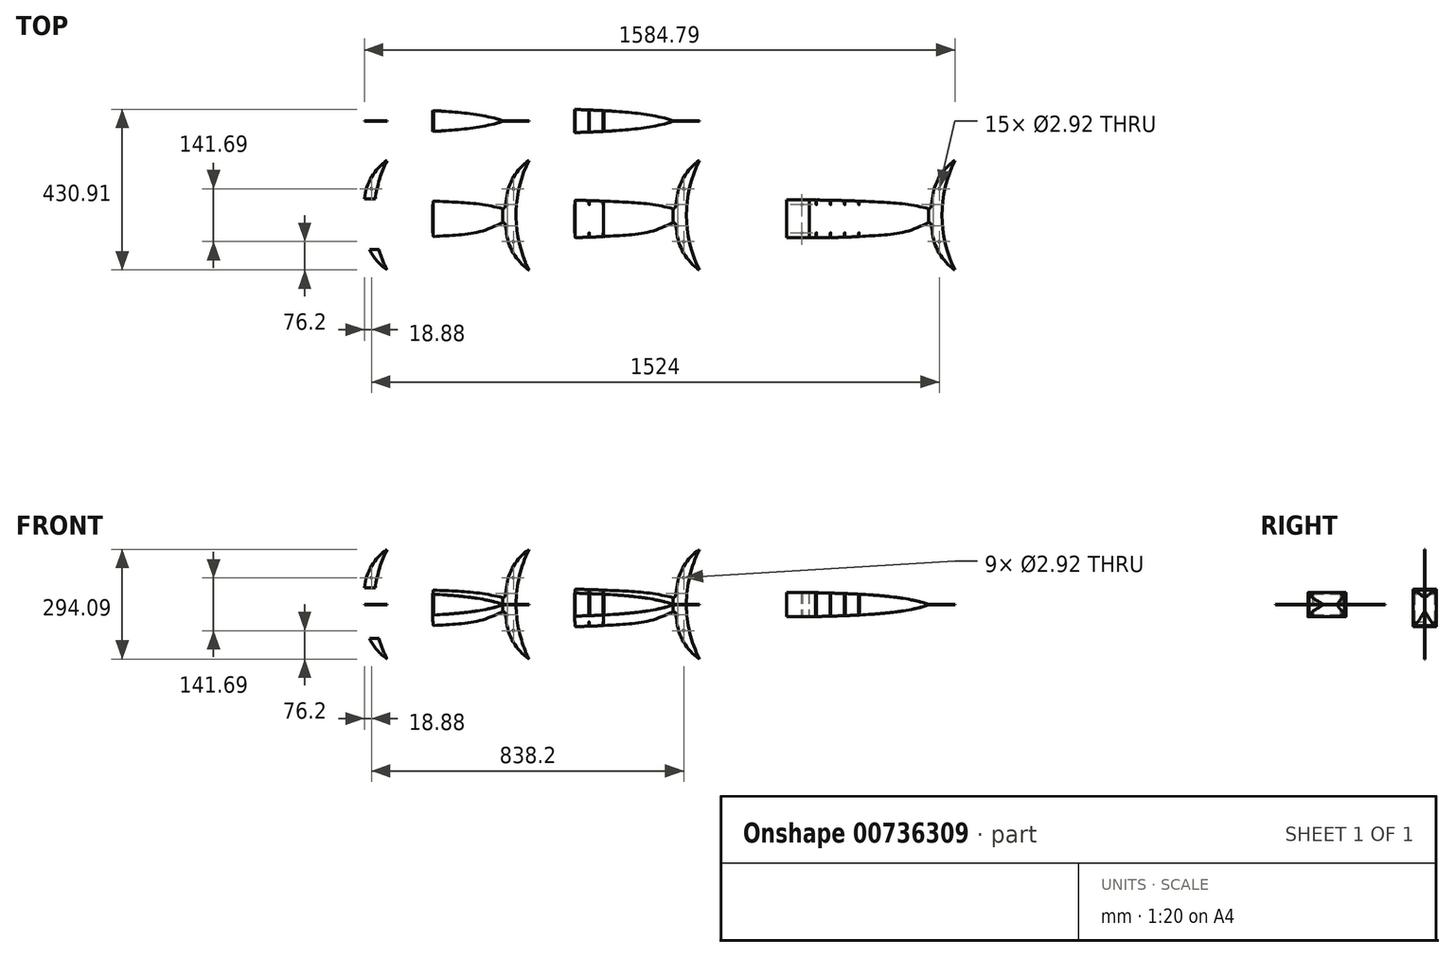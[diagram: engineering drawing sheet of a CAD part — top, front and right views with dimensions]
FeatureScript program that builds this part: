
annotation { "Feature Type Name" : "Feature", "Feature Type Description" : "" }
export const myFeature = defineFeature(function(context is Context, id is Id, definition is map)
    precondition{}
    {
        {
            var Q0;
            Q0=qCreatedBy(makeId("Top.planeOp"),FACE);
            var sketch = newSketch(context, id + "F0", { "sketchPlane" : qUnion([Q0])});
            skArc(sketch, "E0", {"start": v(-213.15, 1.58) * mm, "mid": v(-216.75, 0.09) * mm, "end": v(-218.23, -3.5) * mm});
            skLineSegment(sketch, "E1", {"start": v(-213.15, -100.02) * mm, "end": v(-116.63, -100.02) * mm});
            skLineSegment(sketch, "E2", {"start": v(-218.23, -3.5) * mm, "end": v(-218.23, -94.94) * mm});
            skArc(sketch, "E3", {"start": v(-218.23, -94.94) * mm, "mid": v(-216.75, -98.53) * mm, "end": v(-213.15, -100.02) * mm});
            skArc(sketch, "E4", {"start": v(274.89, 107.35) * mm, "mid": v(233.7, 63.25) * mm, "end": v(214.38, 6.08) * mm});
            skArc(sketch, "E5", {"start": v(214, -81.56) * mm, "mid": v(232.7, -140.95) * mm, "end": v(274.89, -186.74) * mm});
            skArc(sketch, "E6", {"start": v(274.89, 107.35) * mm, "mid": v(240.22, -39.7) * mm, "end": v(274.89, -186.74) * mm});
            skCircle(sketch, "E7", {"center": v(-199.18, -11.12) * mm, "radius": 1.46 * mm});
            skCircle(sketch, "E8", {"center": v(-199.18, -87.32) * mm, "radius": 1.46 * mm});
            skCircle(sketch, "E9", {"center": v(-135.68, -11.12) * mm, "radius": 1.46 * mm});
            skCircle(sketch, "E10", {"center": v(-135.68, -87.32) * mm, "radius": 1.46 * mm});
            skCircle(sketch, "E11", {"center": v(216.74, -11.22) * mm, "radius": 1.46 * mm});
            skCircle(sketch, "E12", {"center": v(216.74, -68.27) * mm, "radius": 1.46 * mm});
            skCircle(sketch, "E13", {"center": v(232.98, 31.15) * mm, "radius": 1.46 * mm});
            skCircle(sketch, "E14", {"center": v(232.98, -110.54) * mm, "radius": 1.46 * mm});
            skLineSegment(sketch, "E15", {"start": v(-116.63, 1.58) * mm, "end": v(-213.15, 1.58) * mm});
            skFitSpline(sketch, "E16", {"points": [v(-116.63, 1.58) * mm, v(-110.7, 1.48) * mm, v(-104.77, 1.39) * mm, v(-98.83, 1.29) * mm]});
            skFitSpline(sketch, "E17", {"points": [v(-95.28, 1.23) * mm, v(-83.76, 1.03) * mm, v(-72.24, 0.83) * mm, v(-60.73, 0.58) * mm]});
            skFitSpline(sketch, "E18", {"points": [v(-57.17, 0.5) * mm, v(-45.64, 0.25) * mm, v(-34.12, -0.04) * mm, v(-22.61, -0.39) * mm]});
            skFitSpline(sketch, "E19", {"points": [v(-19.06, -0.5) * mm, v(-7.53, -0.86) * mm, v(4, -1.29) * mm, v(15.5, -1.8) * mm]});
            skFitSpline(sketch, "E20", {"points": [v(19.06, -1.96) * mm, v(81.46, -4.83) * mm, v(143.45, -10.28) * mm, v(204.47, -21.88) * mm]});
            skFitSpline(sketch, "E21", {"points": [v(-116.63, -100.02) * mm, v(-110.7, -100) * mm, v(-104.77, -99.97) * mm, v(-98.85, -99.94) * mm]});
            skFitSpline(sketch, "E22", {"points": [v(-95.3, -99.92) * mm, v(-83.76, -99.85) * mm, v(-72.24, -99.76) * mm, v(-60.74, -99.6) * mm]});
            skFitSpline(sketch, "E23", {"points": [v(-57.18, -99.55) * mm, v(-45.63, -99.37) * mm, v(-34.1, -99.11) * mm, v(-22.61, -98.74) * mm]});
            skFitSpline(sketch, "E24", {"points": [v(-19.05, -98.62) * mm, v(-7.48, -98.22) * mm, v(4.05, -97.7) * mm, v(15.52, -97) * mm]});
            skFitSpline(sketch, "E25", {"points": [v(19.08, -96.77) * mm, v(83.42, -92.65) * mm, v(145.93, -83) * mm, v(204.03, -59.86) * mm]});
            skLineSegment(sketch, "E26", {"start": v(214.38, 6.08) * mm, "end": v(210.43, -17.72) * mm});
            skLineSegment(sketch, "E27", {"start": v(210.92, -63.72) * mm, "end": v(214, -81.56) * mm});
            skArc(sketch, "E28", {"start": v(204.47, -21.88) * mm, "mid": v(208.32, -21.06) * mm, "end": v(210.43, -17.72) * mm});
            skArc(sketch, "E29", {"start": v(210.92, -63.72) * mm, "mid": v(208.4, -60.15) * mm, "end": v(204.03, -59.86) * mm});
            skLineSegment(sketch, "E30", {"start": v(-97.58, -11.12) * mm, "end": v(-97.58, 0.02) * mm});
            skLineSegment(sketch, "E31", {"start": v(-96.57, -11.12) * mm, "end": v(-96.57, -0.04) * mm});
            skArc(sketch, "E32", {"start": v(-97.58, -11.12) * mm, "mid": v(-97.08, -11.63) * mm, "end": v(-96.57, -11.12) * mm});
            skArc(sketch, "E33", {"start": v(-97.58, 0.02) * mm, "mid": v(-97.95, 0.9) * mm, "end": v(-98.83, 1.29) * mm});
            skArc(sketch, "E34", {"start": v(-95.28, 1.23) * mm, "mid": v(-96.19, 0.86) * mm, "end": v(-96.57, -0.04) * mm});
            skLineSegment(sketch, "E35", {"start": v(-97.58, -87.32) * mm, "end": v(-97.58, -98.67) * mm});
            skLineSegment(sketch, "E36", {"start": v(-96.57, -87.32) * mm, "end": v(-96.57, -98.65) * mm});
            skArc(sketch, "E37", {"start": v(-96.57, -87.32) * mm, "mid": v(-97.08, -86.81) * mm, "end": v(-97.58, -87.32) * mm});
            skArc(sketch, "E38", {"start": v(-98.85, -99.94) * mm, "mid": v(-97.95, -99.57) * mm, "end": v(-97.58, -98.67) * mm});
            skArc(sketch, "E39", {"start": v(-96.57, -98.65) * mm, "mid": v(-96.2, -99.55) * mm, "end": v(-95.3, -99.92) * mm});
            skLineSegment(sketch, "E40", {"start": v(-59.48, -11.12) * mm, "end": v(-59.48, -0.69) * mm});
            skLineSegment(sketch, "E41", {"start": v(-58.47, -11.12) * mm, "end": v(-58.47, -0.76) * mm});
            skArc(sketch, "E42", {"start": v(-59.48, -11.12) * mm, "mid": v(-58.98, -11.63) * mm, "end": v(-58.47, -11.12) * mm});
            skArc(sketch, "E43", {"start": v(-59.48, -0.69) * mm, "mid": v(-59.85, 0.2) * mm, "end": v(-60.73, 0.58) * mm});
            skArc(sketch, "E44", {"start": v(-57.17, 0.5) * mm, "mid": v(-58.09, 0.14) * mm, "end": v(-58.47, -0.76) * mm});
            skLineSegment(sketch, "E45", {"start": v(-59.48, -87.32) * mm, "end": v(-59.48, -98.33) * mm});
            skLineSegment(sketch, "E46", {"start": v(-58.47, -87.32) * mm, "end": v(-58.47, -98.28) * mm});
            skArc(sketch, "E47", {"start": v(-58.47, -87.32) * mm, "mid": v(-58.98, -86.81) * mm, "end": v(-59.48, -87.32) * mm});
            skArc(sketch, "E48", {"start": v(-60.74, -99.6) * mm, "mid": v(-59.85, -99.22) * mm, "end": v(-59.48, -98.33) * mm});
            skArc(sketch, "E49", {"start": v(-58.47, -98.28) * mm, "mid": v(-58.09, -99.18) * mm, "end": v(-57.18, -99.55) * mm});
            skLineSegment(sketch, "E50", {"start": v(-21.38, -11.12) * mm, "end": v(-21.38, -1.65) * mm});
            skLineSegment(sketch, "E51", {"start": v(-20.37, -11.12) * mm, "end": v(-20.37, -1.77) * mm});
            skLineSegment(sketch, "E52", {"start": v(-21.38, -87.32) * mm, "end": v(-21.38, -97.47) * mm});
            skLineSegment(sketch, "E53", {"start": v(-20.37, -87.32) * mm, "end": v(-20.37, -97.35) * mm});
            skLineSegment(sketch, "E54", {"start": v(16.72, -11.12) * mm, "end": v(16.72, -3.07) * mm});
            skLineSegment(sketch, "E55", {"start": v(17.73, -11.12) * mm, "end": v(17.73, -3.23) * mm});
            skLineSegment(sketch, "E56", {"start": v(16.72, -87.32) * mm, "end": v(16.72, -95.73) * mm});
            skLineSegment(sketch, "E57", {"start": v(17.73, -87.32) * mm, "end": v(17.73, -95.5) * mm});
            skArc(sketch, "E58", {"start": v(-21.38, -11.12) * mm, "mid": v(-20.88, -11.63) * mm, "end": v(-20.37, -11.12) * mm});
            skArc(sketch, "E59", {"start": v(16.72, -11.12) * mm, "mid": v(17.22, -11.63) * mm, "end": v(17.73, -11.12) * mm});
            skArc(sketch, "E60", {"start": v(17.73, -87.32) * mm, "mid": v(17.22, -86.81) * mm, "end": v(16.72, -87.32) * mm});
            skArc(sketch, "E61", {"start": v(-20.37, -87.32) * mm, "mid": v(-20.88, -86.81) * mm, "end": v(-21.38, -87.32) * mm});
            skArc(sketch, "E62", {"start": v(-19.06, -0.5) * mm, "mid": v(-19.98, -0.85) * mm, "end": v(-20.37, -1.77) * mm});
            skArc(sketch, "E63", {"start": v(-21.38, -1.65) * mm, "mid": v(-21.74, -0.77) * mm, "end": v(-22.61, -0.39) * mm});
            skArc(sketch, "E64", {"start": v(16.72, -3.07) * mm, "mid": v(16.36, -2.19) * mm, "end": v(15.5, -1.8) * mm});
            skArc(sketch, "E65", {"start": v(19.06, -1.96) * mm, "mid": v(18.13, -2.3) * mm, "end": v(17.73, -3.23) * mm});
            skArc(sketch, "E66", {"start": v(15.52, -97) * mm, "mid": v(16.37, -96.6) * mm, "end": v(16.72, -95.73) * mm});
            skArc(sketch, "E67", {"start": v(17.73, -95.5) * mm, "mid": v(18.13, -96.43) * mm, "end": v(19.08, -96.77) * mm});
            skArc(sketch, "E68", {"start": v(-22.61, -98.74) * mm, "mid": v(-21.74, -98.36) * mm, "end": v(-21.38, -97.47) * mm});
            skArc(sketch, "E69", {"start": v(-20.37, -97.35) * mm, "mid": v(-19.98, -98.27) * mm, "end": v(-19.05, -98.62) * mm});
            skArc(sketch, "E70", {"start": v(201.54, 0.54) * mm, "mid": v(204.92, 1.83) * mm, "end": v(206.59, 5.04) * mm});
            skLineSegment(sketch, "E71", {"start": v(206.62, 5.62) * mm, "end": v(206.62, 97.06) * mm});
            skCircle(sketch, "E72", {"center": v(187.57, 13.24) * mm, "radius": 1.46 * mm});
            skCircle(sketch, "E73", {"center": v(124.07, 13.24) * mm, "radius": 1.46 * mm});
            skLineSegment(sketch, "E74", {"start": v(105.02, 0.54) * mm, "end": v(201.54, 0.54) * mm});
            skFitSpline(sketch, "E75", {"points": [v(105.02, 0.54) * mm, v(99.09, 0.63) * mm, v(93.15, 0.73) * mm, v(87.22, 0.83) * mm]});
            skFitSpline(sketch, "E76", {"points": [v(83.66, 0.89) * mm, v(72.14, 1.08) * mm, v(60.63, 1.29) * mm, v(49.11, 1.53) * mm]});
            skFitSpline(sketch, "E77", {"points": [v(45.56, 1.6) * mm, v(34.03, 1.86) * mm, v(22.51, 2.15) * mm, v(11, 2.5) * mm]});
            skFitSpline(sketch, "E78", {"points": [v(7.44, 2.6) * mm, v(-4.09, 2.97) * mm, v(-15.6, 3.4) * mm, v(-27.12, 3.91) * mm]});
            skLineSegment(sketch, "E79", {"start": v(-226, -3.97) * mm, "end": v(-222.04, 19.84) * mm});
            skLineSegment(sketch, "E80", {"start": v(85.97, 13.24) * mm, "end": v(85.97, 2.1) * mm});
            skLineSegment(sketch, "E81", {"start": v(84.95, 13.24) * mm, "end": v(84.95, 2.16) * mm});
            skArc(sketch, "E82", {"start": v(85.97, 13.24) * mm, "mid": v(85.46, 13.74) * mm, "end": v(84.95, 13.24) * mm});
            skArc(sketch, "E83", {"start": v(85.97, 2.1) * mm, "mid": v(86.34, 1.2) * mm, "end": v(87.22, 0.83) * mm});
            skArc(sketch, "E84", {"start": v(83.66, 0.89) * mm, "mid": v(84.58, 1.25) * mm, "end": v(84.95, 2.16) * mm});
            skLineSegment(sketch, "E85", {"start": v(47.87, 13.24) * mm, "end": v(47.87, 2.8) * mm});
            skLineSegment(sketch, "E86", {"start": v(46.85, 13.24) * mm, "end": v(46.85, 2.88) * mm});
            skArc(sketch, "E87", {"start": v(47.87, 13.24) * mm, "mid": v(47.36, 13.74) * mm, "end": v(46.85, 13.24) * mm});
            skArc(sketch, "E88", {"start": v(47.87, 2.8) * mm, "mid": v(48.23, 1.91) * mm, "end": v(49.11, 1.53) * mm});
            skArc(sketch, "E89", {"start": v(45.56, 1.6) * mm, "mid": v(46.47, 1.97) * mm, "end": v(46.85, 2.88) * mm});
            skLineSegment(sketch, "E90", {"start": v(9.77, 13.24) * mm, "end": v(9.77, 3.77) * mm});
            skLineSegment(sketch, "E91", {"start": v(8.75, 13.24) * mm, "end": v(8.75, 3.88) * mm});
            skLineSegment(sketch, "E92", {"start": v(-28.33, 13.24) * mm, "end": v(-28.33, 5.18) * mm});
            skLineSegment(sketch, "E93", {"start": v(-29.35, 13.24) * mm, "end": v(-29.35, 5.34) * mm});
            skArc(sketch, "E94", {"start": v(9.77, 13.24) * mm, "mid": v(9.26, 13.74) * mm, "end": v(8.75, 13.24) * mm});
            skArc(sketch, "E95", {"start": v(-28.33, 13.24) * mm, "mid": v(-28.84, 13.74) * mm, "end": v(-29.35, 13.24) * mm});
            skArc(sketch, "E96", {"start": v(7.44, 2.6) * mm, "mid": v(8.37, 2.97) * mm, "end": v(8.75, 3.88) * mm});
            skArc(sketch, "E97", {"start": v(9.77, 3.77) * mm, "mid": v(10.13, 2.88) * mm, "end": v(11, 2.5) * mm});
            skArc(sketch, "E98", {"start": v(-28.33, 5.18) * mm, "mid": v(-27.98, 4.3) * mm, "end": v(-27.12, 3.91) * mm});
            skArc(sketch, "E99", {"start": v(-30.67, 4.07) * mm, "mid": v(-29.74, 4.42) * mm, "end": v(-29.35, 5.34) * mm});
            skSolve(sketch);
        }
        {
            var Q0;
            Q0 = qSketchRegion(id + "F0", true);
            extrude(context, id + "F1", {"entities" : qUnion([Q0]), "depth" : 32.5 * mm, "offsetDistance" : 25.4 * mm});
        }
        {
            var Q0;
            Q0=makeQuery(id+"F1.opExtrude","SWEPT_BODY",BODY,{"disambiguationData":[OSD([sQuery(id+"F0.wireOp",EDGE,"E72")])]});
            var Q1;
            Q1=makeQuery(id+"F1.opExtrude","SWEPT_BODY",BODY,{"disambiguationData":[OSD([sQuery(id+"F0.wireOp",EDGE,"E73")])]});
            deleteBodies(context, id + "F2", {"entities" : qUnion([Q0, Q1])});
        }
        {
            var Q0;
            Q0=qCreatedBy(makeId("Front.planeOp"),FACE);
            var sketch = newSketch(context, id + "F3", { "sketchPlane" : qUnion([Q0])});
            skLineSegment(sketch, "E100.0", {"start": v(274.89, 0) * mm, "end": v(214.38, 0) * mm});
            skLineSegment(sketch, "E101.0", {"start": v(204.47, 0) * mm, "end": v(210.43, 0) * mm});
            skLineSegment(sketch, "E102.0", {"start": v(214.38, 0) * mm, "end": v(210.43, 0) * mm});
            skLineSegment(sketch, "E103.0", {"start": v(-213.15, 32.51) * mm, "end": v(-218.23, 32.51) * mm});
            skLineSegment(sketch, "E104.0", {"start": v(-116.63, 32.51) * mm, "end": v(-213.15, 32.51) * mm});
            skLineSegment(sketch, "E105", {"start": v(-218.23, 32.51) * mm, "end": v(-218.23, 31.75) * mm});
            skLineSegment(sketch, "E106", {"start": v(-218.23, 31.75) * mm, "end": v(-116.63, 31.75) * mm});
            skLineSegment(sketch, "E107", {"start": v(274.89, 0) * mm, "end": v(274.89, 0.76) * mm});
            skLineSegment(sketch, "E108", {"start": v(274.89, 0.76) * mm, "end": v(204.47, 0.76) * mm});
            skFitSpline(sketch, "E109", {"points": [v(-116.63, 32.51) * mm, v(204.47, 0.76) * mm, v(299.9, -60.17) * mm], "startDerivative": vector(591.31, -15) * mm, "endDerivative": vector(209.17, -184.85) * mm});
            skFitSpline(sketch, "E110.0", {"points": [v(-116.65, 31.75) * mm, v(-92.01, 31.12) * mm, v(-42.74, 29.87) * mm, v(28.78, 26.94) * mm, v(95.52, 21.9) * mm, v(145.19, 15.06) * mm, v(180.14, 7.48) * mm, v(203.67, 0.62) * mm, v(224.2, -7.56) * mm, v(248.23, -19.95) * mm, v(273.28, -37.65) * mm, v(290.69, -53.04) * mm, v(299.4, -60.74) * mm]});
            skLineSegment(sketch, "E111", {"start": v(204.22, 0.04) * mm, "end": v(204.47, 0) * mm});
            skLineSegment(sketch, "E112.0", {"start": v(-218.23, 32.51) * mm, "end": v(-218.23, 0) * mm});
            skLineSegment(sketch, "E113", {"start": v(-218.23, 0) * mm, "end": v(204.47, 0) * mm});
            skLineSegment(sketch, "E114", {"start": v(-116.63, 32.51) * mm, "end": v(275.65, 32.51) * mm});
            skLineSegment(sketch, "E115", {"start": v(275.65, 32.51) * mm, "end": v(275.65, -7.5) * mm});
            skLineSegment(sketch, "E116", {"start": v(274.89, 0) * mm, "end": v(275.65, 0) * mm});
            skSolve(sketch);
        }
        {
            var Q0;
            Q0=makeQuery(id+"F3.imprint","IMPRINT",FACE,{"disambiguationData":[TD([[makeQuery(id+"F3.imprint","IMPRINT",EDGE,{"derivedFrom":sQuery(id+"F3.wireOp",EDGE,"E107")}),-1.0]])]});
            var Q1;
            {var subQ4=sQuery(id+"F3.wireOp",EDGE,"E111");Q1=makeQuery(id+"F3.imprint","IMPRINT",FACE,{"disambiguationData":[TD([[makeQuery(id+"F3.imprint","IMPRINT",EDGE,{"derivedFrom":subQ4}),-1.0]])]});}
            extrude(context, id + "F4", {"entities" : qUnion([Q0, Q1]), "operationType" : NewBodyOperationType.REMOVE, "endBound" : BoundingType.SYMMETRIC, "oppositeDirection" : true, "depth" : 508 * mm, "offsetDistance" : 25.4 * mm});
        }
        {
            var Q0;
            Q0=makeQuery(id+"F1.opExtrude","SWEPT_BODY",BODY,{"disambiguationData":[OSD([sQuery(id+"F0.wireOp",EDGE,"E0"),sQuery(id+"F0.wireOp",EDGE,"E1"),sQuery(id+"F0.wireOp",EDGE,"E2"),sQuery(id+"F0.wireOp",EDGE,"E3"),sQuery(id+"F0.wireOp",EDGE,"E4"),sQuery(id+"F0.wireOp",EDGE,"E5"),sQuery(id+"F0.wireOp",EDGE,"E6"),sQuery(id+"F0.wireOp",EDGE,"E7"),sQuery(id+"F0.wireOp",EDGE,"E8"),sQuery(id+"F0.wireOp",EDGE,"E9"),sQuery(id+"F0.wireOp",EDGE,"E10"),sQuery(id+"F0.wireOp",EDGE,"E11"),sQuery(id+"F0.wireOp",EDGE,"E12"),sQuery(id+"F0.wireOp",EDGE,"E13"),sQuery(id+"F0.wireOp",EDGE,"E14"),sQuery(id+"F0.wireOp",EDGE,"E15"),sQuery(id+"F0.wireOp",EDGE,"E16"),sQuery(id+"F0.wireOp",EDGE,"E17"),sQuery(id+"F0.wireOp",EDGE,"E18"),sQuery(id+"F0.wireOp",EDGE,"E19"),sQuery(id+"F0.wireOp",EDGE,"E20"),sQuery(id+"F0.wireOp",EDGE,"E21"),sQuery(id+"F0.wireOp",EDGE,"E22"),sQuery(id+"F0.wireOp",EDGE,"E23"),sQuery(id+"F0.wireOp",EDGE,"E24"),sQuery(id+"F0.wireOp",EDGE,"E25"),sQuery(id+"F0.wireOp",EDGE,"E26"),sQuery(id+"F0.wireOp",EDGE,"E27"),sQuery(id+"F0.wireOp",EDGE,"E28"),sQuery(id+"F0.wireOp",EDGE,"E29"),sQuery(id+"F0.wireOp",EDGE,"E30"),sQuery(id+"F0.wireOp",EDGE,"E31"),sQuery(id+"F0.wireOp",EDGE,"E32"),sQuery(id+"F0.wireOp",EDGE,"E33"),sQuery(id+"F0.wireOp",EDGE,"E34"),sQuery(id+"F0.wireOp",EDGE,"E35"),sQuery(id+"F0.wireOp",EDGE,"E36"),sQuery(id+"F0.wireOp",EDGE,"E37"),sQuery(id+"F0.wireOp",EDGE,"E38"),sQuery(id+"F0.wireOp",EDGE,"E39"),sQuery(id+"F0.wireOp",EDGE,"E40"),sQuery(id+"F0.wireOp",EDGE,"E41"),sQuery(id+"F0.wireOp",EDGE,"E42"),sQuery(id+"F0.wireOp",EDGE,"E43"),sQuery(id+"F0.wireOp",EDGE,"E44"),sQuery(id+"F0.wireOp",EDGE,"E45"),sQuery(id+"F0.wireOp",EDGE,"E46"),sQuery(id+"F0.wireOp",EDGE,"E47"),sQuery(id+"F0.wireOp",EDGE,"E48"),sQuery(id+"F0.wireOp",EDGE,"E49"),sQuery(id+"F0.wireOp",EDGE,"E50"),sQuery(id+"F0.wireOp",EDGE,"E51"),sQuery(id+"F0.wireOp",EDGE,"E52"),sQuery(id+"F0.wireOp",EDGE,"E53"),sQuery(id+"F0.wireOp",EDGE,"E54"),sQuery(id+"F0.wireOp",EDGE,"E55"),sQuery(id+"F0.wireOp",EDGE,"E56"),sQuery(id+"F0.wireOp",EDGE,"E57"),sQuery(id+"F0.wireOp",EDGE,"E58"),sQuery(id+"F0.wireOp",EDGE,"E59"),sQuery(id+"F0.wireOp",EDGE,"E60"),sQuery(id+"F0.wireOp",EDGE,"E61"),sQuery(id+"F0.wireOp",EDGE,"E62"),sQuery(id+"F0.wireOp",EDGE,"E63"),sQuery(id+"F0.wireOp",EDGE,"E64"),sQuery(id+"F0.wireOp",EDGE,"E65"),sQuery(id+"F0.wireOp",EDGE,"E66"),sQuery(id+"F0.wireOp",EDGE,"E67"),sQuery(id+"F0.wireOp",EDGE,"E68"),sQuery(id+"F0.wireOp",EDGE,"E69")])]});
            var Q1;
            Q1=makeQuery(id+"F1.opExtrude","CAP_FACE",FACE,{"disambiguationData":[OSD([sQuery(id+"F0.wireOp",EDGE,"E0"),sQuery(id+"F0.wireOp",EDGE,"E1"),sQuery(id+"F0.wireOp",EDGE,"E2"),sQuery(id+"F0.wireOp",EDGE,"E3"),sQuery(id+"F0.wireOp",EDGE,"E4"),sQuery(id+"F0.wireOp",EDGE,"E5"),sQuery(id+"F0.wireOp",EDGE,"E6"),sQuery(id+"F0.wireOp",EDGE,"E7"),sQuery(id+"F0.wireOp",EDGE,"E8"),sQuery(id+"F0.wireOp",EDGE,"E9"),sQuery(id+"F0.wireOp",EDGE,"E10"),sQuery(id+"F0.wireOp",EDGE,"E11"),sQuery(id+"F0.wireOp",EDGE,"E12"),sQuery(id+"F0.wireOp",EDGE,"E13"),sQuery(id+"F0.wireOp",EDGE,"E14"),sQuery(id+"F0.wireOp",EDGE,"E15"),sQuery(id+"F0.wireOp",EDGE,"E16"),sQuery(id+"F0.wireOp",EDGE,"E17"),sQuery(id+"F0.wireOp",EDGE,"E18"),sQuery(id+"F0.wireOp",EDGE,"E19"),sQuery(id+"F0.wireOp",EDGE,"E20"),sQuery(id+"F0.wireOp",EDGE,"E21"),sQuery(id+"F0.wireOp",EDGE,"E22"),sQuery(id+"F0.wireOp",EDGE,"E23"),sQuery(id+"F0.wireOp",EDGE,"E24"),sQuery(id+"F0.wireOp",EDGE,"E25"),sQuery(id+"F0.wireOp",EDGE,"E26"),sQuery(id+"F0.wireOp",EDGE,"E27"),sQuery(id+"F0.wireOp",EDGE,"E28"),sQuery(id+"F0.wireOp",EDGE,"E29"),sQuery(id+"F0.wireOp",EDGE,"E30"),sQuery(id+"F0.wireOp",EDGE,"E31"),sQuery(id+"F0.wireOp",EDGE,"E32"),sQuery(id+"F0.wireOp",EDGE,"E33"),sQuery(id+"F0.wireOp",EDGE,"E34"),sQuery(id+"F0.wireOp",EDGE,"E35"),sQuery(id+"F0.wireOp",EDGE,"E36"),sQuery(id+"F0.wireOp",EDGE,"E37"),sQuery(id+"F0.wireOp",EDGE,"E38"),sQuery(id+"F0.wireOp",EDGE,"E39"),sQuery(id+"F0.wireOp",EDGE,"E40"),sQuery(id+"F0.wireOp",EDGE,"E41"),sQuery(id+"F0.wireOp",EDGE,"E42"),sQuery(id+"F0.wireOp",EDGE,"E43"),sQuery(id+"F0.wireOp",EDGE,"E44"),sQuery(id+"F0.wireOp",EDGE,"E45"),sQuery(id+"F0.wireOp",EDGE,"E46"),sQuery(id+"F0.wireOp",EDGE,"E47"),sQuery(id+"F0.wireOp",EDGE,"E48"),sQuery(id+"F0.wireOp",EDGE,"E49"),sQuery(id+"F0.wireOp",EDGE,"E50"),sQuery(id+"F0.wireOp",EDGE,"E51"),sQuery(id+"F0.wireOp",EDGE,"E52"),sQuery(id+"F0.wireOp",EDGE,"E53"),sQuery(id+"F0.wireOp",EDGE,"E54"),sQuery(id+"F0.wireOp",EDGE,"E55"),sQuery(id+"F0.wireOp",EDGE,"E56"),sQuery(id+"F0.wireOp",EDGE,"E57"),sQuery(id+"F0.wireOp",EDGE,"E58"),sQuery(id+"F0.wireOp",EDGE,"E59"),sQuery(id+"F0.wireOp",EDGE,"E60"),sQuery(id+"F0.wireOp",EDGE,"E61"),sQuery(id+"F0.wireOp",EDGE,"E62"),sQuery(id+"F0.wireOp",EDGE,"E63"),sQuery(id+"F0.wireOp",EDGE,"E64"),sQuery(id+"F0.wireOp",EDGE,"E65"),sQuery(id+"F0.wireOp",EDGE,"E66"),sQuery(id+"F0.wireOp",EDGE,"E67"),sQuery(id+"F0.wireOp",EDGE,"E68"),sQuery(id+"F0.wireOp",EDGE,"E69")])],"isStart":true});
            mirror(context, id + "F5", {"operationType" : NewBodyOperationType.ADD, "entities" : qUnion([Q0]), "mirrorPlane" : qUnion([Q1])});
        }
        {
            var Q0;
            Q0=makeQuery(id+"F1.opExtrude","SWEPT_BODY",BODY,{"disambiguationData":[OSD([sQuery(id+"F0.wireOp",EDGE,"E0"),sQuery(id+"F0.wireOp",EDGE,"E1"),sQuery(id+"F0.wireOp",EDGE,"E2"),sQuery(id+"F0.wireOp",EDGE,"E3"),sQuery(id+"F0.wireOp",EDGE,"E4"),sQuery(id+"F0.wireOp",EDGE,"E5"),sQuery(id+"F0.wireOp",EDGE,"E6"),sQuery(id+"F0.wireOp",EDGE,"E7"),sQuery(id+"F0.wireOp",EDGE,"E8"),sQuery(id+"F0.wireOp",EDGE,"E9"),sQuery(id+"F0.wireOp",EDGE,"E10"),sQuery(id+"F0.wireOp",EDGE,"E11"),sQuery(id+"F0.wireOp",EDGE,"E12"),sQuery(id+"F0.wireOp",EDGE,"E13"),sQuery(id+"F0.wireOp",EDGE,"E14"),sQuery(id+"F0.wireOp",EDGE,"E15"),sQuery(id+"F0.wireOp",EDGE,"E16"),sQuery(id+"F0.wireOp",EDGE,"E17"),sQuery(id+"F0.wireOp",EDGE,"E18"),sQuery(id+"F0.wireOp",EDGE,"E19"),sQuery(id+"F0.wireOp",EDGE,"E20"),sQuery(id+"F0.wireOp",EDGE,"E21"),sQuery(id+"F0.wireOp",EDGE,"E22"),sQuery(id+"F0.wireOp",EDGE,"E23"),sQuery(id+"F0.wireOp",EDGE,"E24"),sQuery(id+"F0.wireOp",EDGE,"E25"),sQuery(id+"F0.wireOp",EDGE,"E26"),sQuery(id+"F0.wireOp",EDGE,"E27"),sQuery(id+"F0.wireOp",EDGE,"E28"),sQuery(id+"F0.wireOp",EDGE,"E29"),sQuery(id+"F0.wireOp",EDGE,"E30"),sQuery(id+"F0.wireOp",EDGE,"E31"),sQuery(id+"F0.wireOp",EDGE,"E32"),sQuery(id+"F0.wireOp",EDGE,"E33"),sQuery(id+"F0.wireOp",EDGE,"E34"),sQuery(id+"F0.wireOp",EDGE,"E35"),sQuery(id+"F0.wireOp",EDGE,"E36"),sQuery(id+"F0.wireOp",EDGE,"E37"),sQuery(id+"F0.wireOp",EDGE,"E38"),sQuery(id+"F0.wireOp",EDGE,"E39"),sQuery(id+"F0.wireOp",EDGE,"E40"),sQuery(id+"F0.wireOp",EDGE,"E41"),sQuery(id+"F0.wireOp",EDGE,"E42"),sQuery(id+"F0.wireOp",EDGE,"E43"),sQuery(id+"F0.wireOp",EDGE,"E44"),sQuery(id+"F0.wireOp",EDGE,"E45"),sQuery(id+"F0.wireOp",EDGE,"E46"),sQuery(id+"F0.wireOp",EDGE,"E47"),sQuery(id+"F0.wireOp",EDGE,"E48"),sQuery(id+"F0.wireOp",EDGE,"E49"),sQuery(id+"F0.wireOp",EDGE,"E50"),sQuery(id+"F0.wireOp",EDGE,"E51"),sQuery(id+"F0.wireOp",EDGE,"E52"),sQuery(id+"F0.wireOp",EDGE,"E53"),sQuery(id+"F0.wireOp",EDGE,"E54"),sQuery(id+"F0.wireOp",EDGE,"E55"),sQuery(id+"F0.wireOp",EDGE,"E56"),sQuery(id+"F0.wireOp",EDGE,"E57"),sQuery(id+"F0.wireOp",EDGE,"E58"),sQuery(id+"F0.wireOp",EDGE,"E59"),sQuery(id+"F0.wireOp",EDGE,"E60"),sQuery(id+"F0.wireOp",EDGE,"E61"),sQuery(id+"F0.wireOp",EDGE,"E62"),sQuery(id+"F0.wireOp",EDGE,"E63"),sQuery(id+"F0.wireOp",EDGE,"E64"),sQuery(id+"F0.wireOp",EDGE,"E65"),sQuery(id+"F0.wireOp",EDGE,"E66"),sQuery(id+"F0.wireOp",EDGE,"E67"),sQuery(id+"F0.wireOp",EDGE,"E68"),sQuery(id+"F0.wireOp",EDGE,"E69")])]});
            transform(context, id + "F6", {"entities" : qUnion([Q0]), "transformType" : TransformType.TRANSLATION_3D, "dx" : -381 * mm, "dy" : 0 * mm, "dz" : 0 * mm, "makeCopy" : true});
        }
        {
            var Q0;
            Q0=makeQuery(id+"F6.opPattern","COPY",FACE,{"derivedFrom":makeQuery(id+"F4.boolean.opBoolean","COPY",FACE,{"derivedFrom":makeQuery(id+"F4.opExtrude","SWEPT_FACE",FACE,{"disambiguationData":[OSD([sQuery(id+"F3.wireOp",EDGE,"E108")])]})}),"instanceName":"1"});
            var sketch = newSketch(context, id + "F7", { "sketchPlane" : qUnion([Q0])});
            skLineSegment(sketch, "E117.bottom", {"start": v(-176.53, -59.7) * mm, "end": v(-695.87, -59.7) * mm});
            skLineSegment(sketch, "E117.top", {"start": v(-176.53, 164.62) * mm, "end": v(-695.87, 164.62) * mm});
            skLineSegment(sketch, "E117.left", {"start": v(-176.53, -59.7) * mm, "end": v(-176.53, 164.62) * mm});
            skLineSegment(sketch, "E117.right", {"start": v(-695.87, -59.7) * mm, "end": v(-695.87, 164.62) * mm});
            skLineSegment(sketch, "E118.bottom", {"start": v(-176.53, 164.62) * mm, "end": v(-759.53, 164.62) * mm});
            skLineSegment(sketch, "E118.top", {"start": v(-176.53, -311.1) * mm, "end": v(-759.53, -311.1) * mm});
            skLineSegment(sketch, "E118.left", {"start": v(-176.53, 164.62) * mm, "end": v(-176.53, -311.1) * mm});
            skLineSegment(sketch, "E118.right", {"start": v(-759.53, 164.62) * mm, "end": v(-759.53, -311.1) * mm});
            skSolve(sketch);
        }
        {
            var Q0;
            Q0 = qSketchRegion(id + "F7", true);
            extrude(context, id + "F8", {"entities" : qUnion([Q0]), "operationType" : NewBodyOperationType.REMOVE, "endBound" : BoundingType.SYMMETRIC, "oppositeDirection" : true, "depth" : 127 * mm, "offsetDistance" : 25.4 * mm});
        }
        {
            var Q0;
            Q0=makeQuery(id+"F1.opExtrude","SWEPT_BODY",BODY,{"disambiguationData":[OSD([sQuery(id+"F0.wireOp",EDGE,"E0"),sQuery(id+"F0.wireOp",EDGE,"E1"),sQuery(id+"F0.wireOp",EDGE,"E2"),sQuery(id+"F0.wireOp",EDGE,"E3"),sQuery(id+"F0.wireOp",EDGE,"E4"),sQuery(id+"F0.wireOp",EDGE,"E5"),sQuery(id+"F0.wireOp",EDGE,"E6"),sQuery(id+"F0.wireOp",EDGE,"E7"),sQuery(id+"F0.wireOp",EDGE,"E8"),sQuery(id+"F0.wireOp",EDGE,"E9"),sQuery(id+"F0.wireOp",EDGE,"E10"),sQuery(id+"F0.wireOp",EDGE,"E11"),sQuery(id+"F0.wireOp",EDGE,"E12"),sQuery(id+"F0.wireOp",EDGE,"E13"),sQuery(id+"F0.wireOp",EDGE,"E14"),sQuery(id+"F0.wireOp",EDGE,"E15"),sQuery(id+"F0.wireOp",EDGE,"E16"),sQuery(id+"F0.wireOp",EDGE,"E17"),sQuery(id+"F0.wireOp",EDGE,"E18"),sQuery(id+"F0.wireOp",EDGE,"E19"),sQuery(id+"F0.wireOp",EDGE,"E20"),sQuery(id+"F0.wireOp",EDGE,"E21"),sQuery(id+"F0.wireOp",EDGE,"E22"),sQuery(id+"F0.wireOp",EDGE,"E23"),sQuery(id+"F0.wireOp",EDGE,"E24"),sQuery(id+"F0.wireOp",EDGE,"E25"),sQuery(id+"F0.wireOp",EDGE,"E26"),sQuery(id+"F0.wireOp",EDGE,"E27"),sQuery(id+"F0.wireOp",EDGE,"E28"),sQuery(id+"F0.wireOp",EDGE,"E29"),sQuery(id+"F0.wireOp",EDGE,"E30"),sQuery(id+"F0.wireOp",EDGE,"E31"),sQuery(id+"F0.wireOp",EDGE,"E32"),sQuery(id+"F0.wireOp",EDGE,"E33"),sQuery(id+"F0.wireOp",EDGE,"E34"),sQuery(id+"F0.wireOp",EDGE,"E35"),sQuery(id+"F0.wireOp",EDGE,"E36"),sQuery(id+"F0.wireOp",EDGE,"E37"),sQuery(id+"F0.wireOp",EDGE,"E38"),sQuery(id+"F0.wireOp",EDGE,"E39"),sQuery(id+"F0.wireOp",EDGE,"E40"),sQuery(id+"F0.wireOp",EDGE,"E41"),sQuery(id+"F0.wireOp",EDGE,"E42"),sQuery(id+"F0.wireOp",EDGE,"E43"),sQuery(id+"F0.wireOp",EDGE,"E44"),sQuery(id+"F0.wireOp",EDGE,"E45"),sQuery(id+"F0.wireOp",EDGE,"E46"),sQuery(id+"F0.wireOp",EDGE,"E47"),sQuery(id+"F0.wireOp",EDGE,"E48"),sQuery(id+"F0.wireOp",EDGE,"E49"),sQuery(id+"F0.wireOp",EDGE,"E50"),sQuery(id+"F0.wireOp",EDGE,"E51"),sQuery(id+"F0.wireOp",EDGE,"E52"),sQuery(id+"F0.wireOp",EDGE,"E53"),sQuery(id+"F0.wireOp",EDGE,"E54"),sQuery(id+"F0.wireOp",EDGE,"E55"),sQuery(id+"F0.wireOp",EDGE,"E56"),sQuery(id+"F0.wireOp",EDGE,"E57"),sQuery(id+"F0.wireOp",EDGE,"E58"),sQuery(id+"F0.wireOp",EDGE,"E59"),sQuery(id+"F0.wireOp",EDGE,"E60"),sQuery(id+"F0.wireOp",EDGE,"E61"),sQuery(id+"F0.wireOp",EDGE,"E62"),sQuery(id+"F0.wireOp",EDGE,"E63"),sQuery(id+"F0.wireOp",EDGE,"E64"),sQuery(id+"F0.wireOp",EDGE,"E65"),sQuery(id+"F0.wireOp",EDGE,"E66"),sQuery(id+"F0.wireOp",EDGE,"E67"),sQuery(id+"F0.wireOp",EDGE,"E68"),sQuery(id+"F0.wireOp",EDGE,"E69")])]});
            transform(context, id + "F9", {"entities" : qUnion([Q0]), "transformType" : TransformType.TRANSLATION_3D, "dx" : 508 * mm, "dy" : 0 * mm, "dz" : 0 * mm, "makeCopy" : true});
        }
        {
            var Q0;
            Q0=qCreatedBy(makeId("Top.planeOp"),FACE);
            var sketch = newSketch(context, id + "F10", { "sketchPlane" : qUnion([Q0])});
            skLineSegment(sketch, "E119.0", {"start": v(16.72, -3.07) * mm, "end": v(16.72, -11.12) * mm});
            skLineSegment(sketch, "E120.bottom", {"start": v(16.72, 4.38) * mm, "end": v(-233.82, 4.38) * mm});
            skLineSegment(sketch, "E120.top", {"start": v(16.72, -131.95) * mm, "end": v(-233.82, -131.95) * mm});
            skLineSegment(sketch, "E120.left", {"start": v(16.72, 4.38) * mm, "end": v(16.72, -131.95) * mm});
            skLineSegment(sketch, "E120.right", {"start": v(-233.82, 4.38) * mm, "end": v(-233.82, -131.95) * mm});
            skSolve(sketch);
        }
        {
            var Q0;
            Q0 = qSketchRegion(id + "F10", true);
            extrude(context, id + "F11", {"entities" : qUnion([Q0]), "operationType" : NewBodyOperationType.REMOVE, "endBound" : BoundingType.SYMMETRIC, "oppositeDirection" : true, "depth" : 127 * mm, "offsetDistance" : 25.4 * mm});
        }
        {
            var Q0;
            Q0=makeQuery(id+"F9.opPattern","COPY",BODY,{"derivedFrom":makeQuery(id+"F1.opExtrude","SWEPT_BODY",BODY,{"disambiguationData":[OSD([sQuery(id+"F0.wireOp",EDGE,"E0"),sQuery(id+"F0.wireOp",EDGE,"E1"),sQuery(id+"F0.wireOp",EDGE,"E2"),sQuery(id+"F0.wireOp",EDGE,"E3"),sQuery(id+"F0.wireOp",EDGE,"E4"),sQuery(id+"F0.wireOp",EDGE,"E5"),sQuery(id+"F0.wireOp",EDGE,"E6"),sQuery(id+"F0.wireOp",EDGE,"E7"),sQuery(id+"F0.wireOp",EDGE,"E8"),sQuery(id+"F0.wireOp",EDGE,"E9"),sQuery(id+"F0.wireOp",EDGE,"E10"),sQuery(id+"F0.wireOp",EDGE,"E11"),sQuery(id+"F0.wireOp",EDGE,"E12"),sQuery(id+"F0.wireOp",EDGE,"E13"),sQuery(id+"F0.wireOp",EDGE,"E14"),sQuery(id+"F0.wireOp",EDGE,"E15"),sQuery(id+"F0.wireOp",EDGE,"E16"),sQuery(id+"F0.wireOp",EDGE,"E17"),sQuery(id+"F0.wireOp",EDGE,"E18"),sQuery(id+"F0.wireOp",EDGE,"E19"),sQuery(id+"F0.wireOp",EDGE,"E20"),sQuery(id+"F0.wireOp",EDGE,"E21"),sQuery(id+"F0.wireOp",EDGE,"E22"),sQuery(id+"F0.wireOp",EDGE,"E23"),sQuery(id+"F0.wireOp",EDGE,"E24"),sQuery(id+"F0.wireOp",EDGE,"E25"),sQuery(id+"F0.wireOp",EDGE,"E26"),sQuery(id+"F0.wireOp",EDGE,"E27"),sQuery(id+"F0.wireOp",EDGE,"E28"),sQuery(id+"F0.wireOp",EDGE,"E29"),sQuery(id+"F0.wireOp",EDGE,"E30"),sQuery(id+"F0.wireOp",EDGE,"E31"),sQuery(id+"F0.wireOp",EDGE,"E32"),sQuery(id+"F0.wireOp",EDGE,"E33"),sQuery(id+"F0.wireOp",EDGE,"E34"),sQuery(id+"F0.wireOp",EDGE,"E35"),sQuery(id+"F0.wireOp",EDGE,"E36"),sQuery(id+"F0.wireOp",EDGE,"E37"),sQuery(id+"F0.wireOp",EDGE,"E38"),sQuery(id+"F0.wireOp",EDGE,"E39"),sQuery(id+"F0.wireOp",EDGE,"E40"),sQuery(id+"F0.wireOp",EDGE,"E41"),sQuery(id+"F0.wireOp",EDGE,"E42"),sQuery(id+"F0.wireOp",EDGE,"E43"),sQuery(id+"F0.wireOp",EDGE,"E44"),sQuery(id+"F0.wireOp",EDGE,"E45"),sQuery(id+"F0.wireOp",EDGE,"E46"),sQuery(id+"F0.wireOp",EDGE,"E47"),sQuery(id+"F0.wireOp",EDGE,"E48"),sQuery(id+"F0.wireOp",EDGE,"E49"),sQuery(id+"F0.wireOp",EDGE,"E50"),sQuery(id+"F0.wireOp",EDGE,"E51"),sQuery(id+"F0.wireOp",EDGE,"E52"),sQuery(id+"F0.wireOp",EDGE,"E53"),sQuery(id+"F0.wireOp",EDGE,"E54"),sQuery(id+"F0.wireOp",EDGE,"E55"),sQuery(id+"F0.wireOp",EDGE,"E56"),sQuery(id+"F0.wireOp",EDGE,"E57"),sQuery(id+"F0.wireOp",EDGE,"E58"),sQuery(id+"F0.wireOp",EDGE,"E59"),sQuery(id+"F0.wireOp",EDGE,"E60"),sQuery(id+"F0.wireOp",EDGE,"E61"),sQuery(id+"F0.wireOp",EDGE,"E62"),sQuery(id+"F0.wireOp",EDGE,"E63"),sQuery(id+"F0.wireOp",EDGE,"E64"),sQuery(id+"F0.wireOp",EDGE,"E65"),sQuery(id+"F0.wireOp",EDGE,"E66"),sQuery(id+"F0.wireOp",EDGE,"E67"),sQuery(id+"F0.wireOp",EDGE,"E68"),sQuery(id+"F0.wireOp",EDGE,"E69")])]}),"instanceName":"1"});
            transform(context, id + "F12", {"entities" : qUnion([Q0]), "transformType" : TransformType.TRANSLATION_3D, "dx" : 635 * mm, "dy" : 0 * mm, "dz" : 0 * mm, "makeCopy" : true});
        }
        {
            var Q0;
            Q0=qCreatedBy(makeId("Top.planeOp"),FACE);
            var sketch = newSketch(context, id + "F13", { "sketchPlane" : qUnion([Q0])});
            skLineSegment(sketch, "E121.0", {"start": v(448.52, -0.69) * mm, "end": v(448.52, -11.12) * mm});
            skLineSegment(sketch, "E122.bottom", {"start": v(448.52, 15.05) * mm, "end": v(265.19, 15.05) * mm});
            skLineSegment(sketch, "E122.top", {"start": v(448.52, -170.46) * mm, "end": v(265.19, -170.46) * mm});
            skLineSegment(sketch, "E122.left", {"start": v(448.52, 15.05) * mm, "end": v(448.52, -170.46) * mm});
            skLineSegment(sketch, "E122.right", {"start": v(265.19, 15.05) * mm, "end": v(265.19, -170.46) * mm});
            skSolve(sketch);
        }
        {
            var Q0;
            Q0 = qSketchRegion(id + "F13", true);
            extrude(context, id + "F14", {"entities" : qUnion([Q0]), "operationType" : NewBodyOperationType.REMOVE, "endBound" : BoundingType.SYMMETRIC, "oppositeDirection" : true, "depth" : 381 * mm, "offsetDistance" : 25.4 * mm});
        }
        {
            var Q0;
            Q0=makeQuery(id+"F5.opPattern","COPY",FACE,{"derivedFrom":makeQuery(id+"F1.opExtrude","SWEPT_FACE",FACE,{"disambiguationData":[OSD([sQuery(id+"F0.wireOp",EDGE,"E55")])]}),"instanceName":"1"});
            var sketch = newSketch(context, id + "F15", { "sketchPlane" : qUnion([Q0])});
            skLineSegment(sketch, "E123.0", {"start": v(3.23, -27.92) * mm, "end": v(3.23, -27.16) * mm});
            skLineSegment(sketch, "E124.0", {"start": v(3.23, -27.92) * mm, "end": v(11.12, -27.92) * mm});
            skLineSegment(sketch, "E125.top", {"start": v(3.23, -27.16) * mm, "end": v(11.12, -27.16) * mm});
            skLineSegment(sketch, "E125.right", {"start": v(11.12, -27.92) * mm, "end": v(11.12, -27.16) * mm});
            skLineSegment(sketch, "E126.0.0", {"start": v(3.23, 27.92) * mm, "end": v(3.23, 27.16) * mm});
            skLineSegment(sketch, "E126.0.1", {"start": v(3.23, 27.16) * mm, "end": v(11.12, 27.16) * mm});
            skLineSegment(sketch, "E126.0.2", {"start": v(11.12, 27.16) * mm, "end": v(11.12, 27.92) * mm});
            skLineSegment(sketch, "E126.0.3", {"start": v(11.12, 27.92) * mm, "end": v(3.23, 27.92) * mm});
            skLineSegment(sketch, "E127.0.0", {"start": v(95.5, 27.16) * mm, "end": v(87.32, 27.16) * mm});
            skLineSegment(sketch, "E127.0.1", {"start": v(95.5, 27.16) * mm, "end": v(95.5, 27.92) * mm});
            skLineSegment(sketch, "E127.0.2", {"start": v(95.5, 27.92) * mm, "end": v(87.32, 27.92) * mm});
            skLineSegment(sketch, "E127.0.3", {"start": v(87.32, 27.92) * mm, "end": v(87.32, 27.16) * mm});
            skLineSegment(sketch, "E128.0.0", {"start": v(95.5, -27.16) * mm, "end": v(87.32, -27.16) * mm});
            skLineSegment(sketch, "E128.0.1", {"start": v(87.32, -27.16) * mm, "end": v(87.32, -27.92) * mm});
            skLineSegment(sketch, "E128.0.2", {"start": v(95.5, -27.92) * mm, "end": v(87.32, -27.92) * mm});
            skLineSegment(sketch, "E128.0.3", {"start": v(95.5, -27.92) * mm, "end": v(95.5, -27.16) * mm});
            skLineSegment(sketch, "E129", {"start": v(87.32, -27.16) * mm, "end": v(11.12, -27.16) * mm});
            skLineSegment(sketch, "E130", {"start": v(3.23, -27.16) * mm, "end": v(3.23, 27.16) * mm});
            skLineSegment(sketch, "E131", {"start": v(11.12, 27.16) * mm, "end": v(87.32, 27.16) * mm});
            skLineSegment(sketch, "E132", {"start": v(95.5, 27.16) * mm, "end": v(95.5, -27.16) * mm});
            skSolve(sketch);
        }
        {
            var Q0;
            Q0 = qSketchRegion(id + "F15", true);
            extrude(context, id + "F16", {"entities" : qUnion([Q0]), "depth" : 0.76 * mm, "offsetDistance" : 25.4 * mm});
        }
        {
            var Q0;
            Q0=makeQuery(id+"F16.opExtrude","SWEPT_BODY",BODY,{"disambiguationData":[OSD([sQuery(id+"F15.wireOp",EDGE,"E124.0"),sQuery(id+"F15.wireOp",EDGE,"E123.0"),sQuery(id+"F15.wireOp",EDGE,"E125.right"),sQuery(id+"F15.wireOp",EDGE,"E126.0.0"),sQuery(id+"F15.wireOp",EDGE,"E126.0.2"),sQuery(id+"F15.wireOp",EDGE,"E126.0.3"),sQuery(id+"F15.wireOp",EDGE,"E127.0.1"),sQuery(id+"F15.wireOp",EDGE,"E127.0.2"),sQuery(id+"F15.wireOp",EDGE,"E127.0.3"),sQuery(id+"F15.wireOp",EDGE,"E128.0.1"),sQuery(id+"F15.wireOp",EDGE,"E128.0.2"),sQuery(id+"F15.wireOp",EDGE,"E128.0.3"),sQuery(id+"F15.wireOp",EDGE,"E129"),sQuery(id+"F15.wireOp",EDGE,"E130"),sQuery(id+"F15.wireOp",EDGE,"E131"),sQuery(id+"F15.wireOp",EDGE,"E132")])]});
            transform(context, id + "F17", {"entities" : qUnion([Q0]), "transformType" : TransformType.TRANSLATION_3D, "dx" : 508 * mm, "dy" : 0 * mm, "dz" : 0 * mm, "makeCopy" : true});
        }
        {
            var Q0;
            Q0=makeQuery(id+"F9.opPattern","COPY",FACE,{"derivedFrom":makeQuery(id+"F5.opPattern","COPY",FACE,{"derivedFrom":makeQuery(id+"F1.opExtrude","SWEPT_FACE",FACE,{"disambiguationData":[OSD([sQuery(id+"F0.wireOp",EDGE,"E41")])]}),"instanceName":"1"}),"instanceName":"1"});
            var sketch = newSketch(context, id + "F18", { "sketchPlane" : qUnion([Q0])});
            skLineSegment(sketch, "E133.0.0", {"start": v(0.76, -30.18) * mm, "end": v(0.76, -30.94) * mm});
            skLineSegment(sketch, "E133.0.1", {"start": v(0.76, -30.94) * mm, "end": v(11.12, -30.94) * mm});
            skLineSegment(sketch, "E133.0.2", {"start": v(11.12, -30.94) * mm, "end": v(11.12, -30.18) * mm});
            skLineSegment(sketch, "E133.0.3", {"start": v(11.12, -30.18) * mm, "end": v(0.76, -30.18) * mm});
            skLineSegment(sketch, "E134.0.0", {"start": v(0.76, 30.94) * mm, "end": v(0.76, 30.18) * mm});
            skLineSegment(sketch, "E134.0.1", {"start": v(0.76, 30.18) * mm, "end": v(11.12, 30.18) * mm});
            skLineSegment(sketch, "E134.0.2", {"start": v(11.12, 30.18) * mm, "end": v(11.12, 30.94) * mm});
            skLineSegment(sketch, "E134.0.3", {"start": v(11.12, 30.94) * mm, "end": v(0.76, 30.94) * mm});
            skLineSegment(sketch, "E135.0.0", {"start": v(98.28, 30.18) * mm, "end": v(87.32, 30.18) * mm});
            skLineSegment(sketch, "E135.0.1", {"start": v(98.28, 30.18) * mm, "end": v(98.28, 30.94) * mm});
            skLineSegment(sketch, "E135.0.2", {"start": v(98.28, 30.94) * mm, "end": v(87.32, 30.94) * mm});
            skLineSegment(sketch, "E135.0.3", {"start": v(87.32, 30.94) * mm, "end": v(87.32, 30.18) * mm});
            skLineSegment(sketch, "E136.0.0", {"start": v(98.28, -30.18) * mm, "end": v(87.32, -30.18) * mm});
            skLineSegment(sketch, "E136.0.1", {"start": v(87.32, -30.18) * mm, "end": v(87.32, -30.94) * mm});
            skLineSegment(sketch, "E136.0.2", {"start": v(98.28, -30.94) * mm, "end": v(87.32, -30.94) * mm});
            skLineSegment(sketch, "E136.0.3", {"start": v(98.28, -30.94) * mm, "end": v(98.28, -30.18) * mm});
            skLineSegment(sketch, "E137", {"start": v(0.76, -30.18) * mm, "end": v(0.76, 30.18) * mm});
            skLineSegment(sketch, "E138", {"start": v(11.12, 30.18) * mm, "end": v(87.32, 30.18) * mm});
            skLineSegment(sketch, "E139", {"start": v(98.28, 30.18) * mm, "end": v(98.28, -30.18) * mm});
            skLineSegment(sketch, "E140", {"start": v(87.32, -30.18) * mm, "end": v(11.12, -30.18) * mm});
            skSolve(sketch);
        }
        {
            var Q0;
            Q0 = qSketchRegion(id + "F18", true);
            extrude(context, id + "F19", {"entities" : qUnion([Q0]), "depth" : 0.76 * mm, "offsetDistance" : 25.4 * mm});
        }
        {
            var Q0;
            Q0=makeQuery(id+"F17.opPattern","COPY",BODY,{"derivedFrom":makeQuery(id+"F16.opExtrude","SWEPT_BODY",BODY,{"disambiguationData":[OSD([sQuery(id+"F15.wireOp",EDGE,"E124.0"),sQuery(id+"F15.wireOp",EDGE,"E123.0"),sQuery(id+"F15.wireOp",EDGE,"E125.right"),sQuery(id+"F15.wireOp",EDGE,"E126.0.0"),sQuery(id+"F15.wireOp",EDGE,"E126.0.2"),sQuery(id+"F15.wireOp",EDGE,"E126.0.3"),sQuery(id+"F15.wireOp",EDGE,"E127.0.1"),sQuery(id+"F15.wireOp",EDGE,"E127.0.2"),sQuery(id+"F15.wireOp",EDGE,"E127.0.3"),sQuery(id+"F15.wireOp",EDGE,"E128.0.1"),sQuery(id+"F15.wireOp",EDGE,"E128.0.2"),sQuery(id+"F15.wireOp",EDGE,"E128.0.3"),sQuery(id+"F15.wireOp",EDGE,"E129"),sQuery(id+"F15.wireOp",EDGE,"E130"),sQuery(id+"F15.wireOp",EDGE,"E131"),sQuery(id+"F15.wireOp",EDGE,"E132")])]}),"instanceName":"1"});
            var Q1;
            Q1=makeQuery(id+"F9.opPattern","COPY",BODY,{"derivedFrom":makeQuery(id+"F1.opExtrude","SWEPT_BODY",BODY,{"disambiguationData":[OSD([sQuery(id+"F0.wireOp",EDGE,"E0"),sQuery(id+"F0.wireOp",EDGE,"E1"),sQuery(id+"F0.wireOp",EDGE,"E2"),sQuery(id+"F0.wireOp",EDGE,"E3"),sQuery(id+"F0.wireOp",EDGE,"E4"),sQuery(id+"F0.wireOp",EDGE,"E5"),sQuery(id+"F0.wireOp",EDGE,"E6"),sQuery(id+"F0.wireOp",EDGE,"E7"),sQuery(id+"F0.wireOp",EDGE,"E8"),sQuery(id+"F0.wireOp",EDGE,"E9"),sQuery(id+"F0.wireOp",EDGE,"E10"),sQuery(id+"F0.wireOp",EDGE,"E11"),sQuery(id+"F0.wireOp",EDGE,"E12"),sQuery(id+"F0.wireOp",EDGE,"E13"),sQuery(id+"F0.wireOp",EDGE,"E14"),sQuery(id+"F0.wireOp",EDGE,"E15"),sQuery(id+"F0.wireOp",EDGE,"E16"),sQuery(id+"F0.wireOp",EDGE,"E17"),sQuery(id+"F0.wireOp",EDGE,"E18"),sQuery(id+"F0.wireOp",EDGE,"E19"),sQuery(id+"F0.wireOp",EDGE,"E20"),sQuery(id+"F0.wireOp",EDGE,"E21"),sQuery(id+"F0.wireOp",EDGE,"E22"),sQuery(id+"F0.wireOp",EDGE,"E23"),sQuery(id+"F0.wireOp",EDGE,"E24"),sQuery(id+"F0.wireOp",EDGE,"E25"),sQuery(id+"F0.wireOp",EDGE,"E26"),sQuery(id+"F0.wireOp",EDGE,"E27"),sQuery(id+"F0.wireOp",EDGE,"E28"),sQuery(id+"F0.wireOp",EDGE,"E29"),sQuery(id+"F0.wireOp",EDGE,"E30"),sQuery(id+"F0.wireOp",EDGE,"E31"),sQuery(id+"F0.wireOp",EDGE,"E32"),sQuery(id+"F0.wireOp",EDGE,"E33"),sQuery(id+"F0.wireOp",EDGE,"E34"),sQuery(id+"F0.wireOp",EDGE,"E35"),sQuery(id+"F0.wireOp",EDGE,"E36"),sQuery(id+"F0.wireOp",EDGE,"E37"),sQuery(id+"F0.wireOp",EDGE,"E38"),sQuery(id+"F0.wireOp",EDGE,"E39"),sQuery(id+"F0.wireOp",EDGE,"E40"),sQuery(id+"F0.wireOp",EDGE,"E41"),sQuery(id+"F0.wireOp",EDGE,"E42"),sQuery(id+"F0.wireOp",EDGE,"E43"),sQuery(id+"F0.wireOp",EDGE,"E44"),sQuery(id+"F0.wireOp",EDGE,"E45"),sQuery(id+"F0.wireOp",EDGE,"E46"),sQuery(id+"F0.wireOp",EDGE,"E47"),sQuery(id+"F0.wireOp",EDGE,"E48"),sQuery(id+"F0.wireOp",EDGE,"E49"),sQuery(id+"F0.wireOp",EDGE,"E50"),sQuery(id+"F0.wireOp",EDGE,"E51"),sQuery(id+"F0.wireOp",EDGE,"E52"),sQuery(id+"F0.wireOp",EDGE,"E53"),sQuery(id+"F0.wireOp",EDGE,"E54"),sQuery(id+"F0.wireOp",EDGE,"E55"),sQuery(id+"F0.wireOp",EDGE,"E56"),sQuery(id+"F0.wireOp",EDGE,"E57"),sQuery(id+"F0.wireOp",EDGE,"E58"),sQuery(id+"F0.wireOp",EDGE,"E59"),sQuery(id+"F0.wireOp",EDGE,"E60"),sQuery(id+"F0.wireOp",EDGE,"E61"),sQuery(id+"F0.wireOp",EDGE,"E62"),sQuery(id+"F0.wireOp",EDGE,"E63"),sQuery(id+"F0.wireOp",EDGE,"E64"),sQuery(id+"F0.wireOp",EDGE,"E65"),sQuery(id+"F0.wireOp",EDGE,"E66"),sQuery(id+"F0.wireOp",EDGE,"E67"),sQuery(id+"F0.wireOp",EDGE,"E68"),sQuery(id+"F0.wireOp",EDGE,"E69")])]}),"instanceName":"1"});
            var Q2;
            Q2=makeQuery(id+"F19.opExtrude","SWEPT_BODY",BODY,{"disambiguationData":[OSD([sQuery(id+"F18.wireOp",EDGE,"E133.0.0"),sQuery(id+"F18.wireOp",EDGE,"E133.0.1"),sQuery(id+"F18.wireOp",EDGE,"E133.0.2"),sQuery(id+"F18.wireOp",EDGE,"E134.0.0"),sQuery(id+"F18.wireOp",EDGE,"E134.0.2"),sQuery(id+"F18.wireOp",EDGE,"E134.0.3"),sQuery(id+"F18.wireOp",EDGE,"E135.0.1"),sQuery(id+"F18.wireOp",EDGE,"E135.0.2"),sQuery(id+"F18.wireOp",EDGE,"E135.0.3"),sQuery(id+"F18.wireOp",EDGE,"E136.0.1"),sQuery(id+"F18.wireOp",EDGE,"E136.0.2"),sQuery(id+"F18.wireOp",EDGE,"E136.0.3"),sQuery(id+"F18.wireOp",EDGE,"E137"),sQuery(id+"F18.wireOp",EDGE,"E138"),sQuery(id+"F18.wireOp",EDGE,"E139"),sQuery(id+"F18.wireOp",EDGE,"E140")])]});
            transform(context, id + "F20", {"entities" : qUnion([Q0, Q1, Q2]), "transformType" : TransformType.TRANSLATION_3D, "dx" : -50.8 * mm, "dy" : 0 * mm, "dz" : 0 * mm, "makeCopy" : false});
        }
        {
            var Q0;
            Q0=makeQuery(id+"F6.opPattern","COPY",BODY,{"derivedFrom":makeQuery(id+"F1.opExtrude","SWEPT_BODY",BODY,{"disambiguationData":[OSD([sQuery(id+"F0.wireOp",EDGE,"E0"),sQuery(id+"F0.wireOp",EDGE,"E1"),sQuery(id+"F0.wireOp",EDGE,"E2"),sQuery(id+"F0.wireOp",EDGE,"E3"),sQuery(id+"F0.wireOp",EDGE,"E4"),sQuery(id+"F0.wireOp",EDGE,"E5"),sQuery(id+"F0.wireOp",EDGE,"E6"),sQuery(id+"F0.wireOp",EDGE,"E7"),sQuery(id+"F0.wireOp",EDGE,"E8"),sQuery(id+"F0.wireOp",EDGE,"E9"),sQuery(id+"F0.wireOp",EDGE,"E10"),sQuery(id+"F0.wireOp",EDGE,"E11"),sQuery(id+"F0.wireOp",EDGE,"E12"),sQuery(id+"F0.wireOp",EDGE,"E13"),sQuery(id+"F0.wireOp",EDGE,"E14"),sQuery(id+"F0.wireOp",EDGE,"E15"),sQuery(id+"F0.wireOp",EDGE,"E16"),sQuery(id+"F0.wireOp",EDGE,"E17"),sQuery(id+"F0.wireOp",EDGE,"E18"),sQuery(id+"F0.wireOp",EDGE,"E19"),sQuery(id+"F0.wireOp",EDGE,"E20"),sQuery(id+"F0.wireOp",EDGE,"E21"),sQuery(id+"F0.wireOp",EDGE,"E22"),sQuery(id+"F0.wireOp",EDGE,"E23"),sQuery(id+"F0.wireOp",EDGE,"E24"),sQuery(id+"F0.wireOp",EDGE,"E25"),sQuery(id+"F0.wireOp",EDGE,"E26"),sQuery(id+"F0.wireOp",EDGE,"E27"),sQuery(id+"F0.wireOp",EDGE,"E28"),sQuery(id+"F0.wireOp",EDGE,"E29"),sQuery(id+"F0.wireOp",EDGE,"E30"),sQuery(id+"F0.wireOp",EDGE,"E31"),sQuery(id+"F0.wireOp",EDGE,"E32"),sQuery(id+"F0.wireOp",EDGE,"E33"),sQuery(id+"F0.wireOp",EDGE,"E34"),sQuery(id+"F0.wireOp",EDGE,"E35"),sQuery(id+"F0.wireOp",EDGE,"E36"),sQuery(id+"F0.wireOp",EDGE,"E37"),sQuery(id+"F0.wireOp",EDGE,"E38"),sQuery(id+"F0.wireOp",EDGE,"E39"),sQuery(id+"F0.wireOp",EDGE,"E40"),sQuery(id+"F0.wireOp",EDGE,"E41"),sQuery(id+"F0.wireOp",EDGE,"E42"),sQuery(id+"F0.wireOp",EDGE,"E43"),sQuery(id+"F0.wireOp",EDGE,"E44"),sQuery(id+"F0.wireOp",EDGE,"E45"),sQuery(id+"F0.wireOp",EDGE,"E46"),sQuery(id+"F0.wireOp",EDGE,"E47"),sQuery(id+"F0.wireOp",EDGE,"E48"),sQuery(id+"F0.wireOp",EDGE,"E49"),sQuery(id+"F0.wireOp",EDGE,"E50"),sQuery(id+"F0.wireOp",EDGE,"E51"),sQuery(id+"F0.wireOp",EDGE,"E52"),sQuery(id+"F0.wireOp",EDGE,"E53"),sQuery(id+"F0.wireOp",EDGE,"E54"),sQuery(id+"F0.wireOp",EDGE,"E55"),sQuery(id+"F0.wireOp",EDGE,"E56"),sQuery(id+"F0.wireOp",EDGE,"E57"),sQuery(id+"F0.wireOp",EDGE,"E58"),sQuery(id+"F0.wireOp",EDGE,"E59"),sQuery(id+"F0.wireOp",EDGE,"E60"),sQuery(id+"F0.wireOp",EDGE,"E61"),sQuery(id+"F0.wireOp",EDGE,"E62"),sQuery(id+"F0.wireOp",EDGE,"E63"),sQuery(id+"F0.wireOp",EDGE,"E64"),sQuery(id+"F0.wireOp",EDGE,"E65"),sQuery(id+"F0.wireOp",EDGE,"E66"),sQuery(id+"F0.wireOp",EDGE,"E67"),sQuery(id+"F0.wireOp",EDGE,"E68"),sQuery(id+"F0.wireOp",EDGE,"E69")])]}),"instanceName":"1"});
            var Q1;
            Q1=makeQuery(id+"F1.opExtrude","SWEPT_BODY",BODY,{"disambiguationData":[OSD([sQuery(id+"F0.wireOp",EDGE,"E0"),sQuery(id+"F0.wireOp",EDGE,"E1"),sQuery(id+"F0.wireOp",EDGE,"E2"),sQuery(id+"F0.wireOp",EDGE,"E3"),sQuery(id+"F0.wireOp",EDGE,"E4"),sQuery(id+"F0.wireOp",EDGE,"E5"),sQuery(id+"F0.wireOp",EDGE,"E6"),sQuery(id+"F0.wireOp",EDGE,"E7"),sQuery(id+"F0.wireOp",EDGE,"E8"),sQuery(id+"F0.wireOp",EDGE,"E9"),sQuery(id+"F0.wireOp",EDGE,"E10"),sQuery(id+"F0.wireOp",EDGE,"E11"),sQuery(id+"F0.wireOp",EDGE,"E12"),sQuery(id+"F0.wireOp",EDGE,"E13"),sQuery(id+"F0.wireOp",EDGE,"E14"),sQuery(id+"F0.wireOp",EDGE,"E15"),sQuery(id+"F0.wireOp",EDGE,"E16"),sQuery(id+"F0.wireOp",EDGE,"E17"),sQuery(id+"F0.wireOp",EDGE,"E18"),sQuery(id+"F0.wireOp",EDGE,"E19"),sQuery(id+"F0.wireOp",EDGE,"E20"),sQuery(id+"F0.wireOp",EDGE,"E21"),sQuery(id+"F0.wireOp",EDGE,"E22"),sQuery(id+"F0.wireOp",EDGE,"E23"),sQuery(id+"F0.wireOp",EDGE,"E24"),sQuery(id+"F0.wireOp",EDGE,"E25"),sQuery(id+"F0.wireOp",EDGE,"E26"),sQuery(id+"F0.wireOp",EDGE,"E27"),sQuery(id+"F0.wireOp",EDGE,"E28"),sQuery(id+"F0.wireOp",EDGE,"E29"),sQuery(id+"F0.wireOp",EDGE,"E30"),sQuery(id+"F0.wireOp",EDGE,"E31"),sQuery(id+"F0.wireOp",EDGE,"E32"),sQuery(id+"F0.wireOp",EDGE,"E33"),sQuery(id+"F0.wireOp",EDGE,"E34"),sQuery(id+"F0.wireOp",EDGE,"E35"),sQuery(id+"F0.wireOp",EDGE,"E36"),sQuery(id+"F0.wireOp",EDGE,"E37"),sQuery(id+"F0.wireOp",EDGE,"E38"),sQuery(id+"F0.wireOp",EDGE,"E39"),sQuery(id+"F0.wireOp",EDGE,"E40"),sQuery(id+"F0.wireOp",EDGE,"E41"),sQuery(id+"F0.wireOp",EDGE,"E42"),sQuery(id+"F0.wireOp",EDGE,"E43"),sQuery(id+"F0.wireOp",EDGE,"E44"),sQuery(id+"F0.wireOp",EDGE,"E45"),sQuery(id+"F0.wireOp",EDGE,"E46"),sQuery(id+"F0.wireOp",EDGE,"E47"),sQuery(id+"F0.wireOp",EDGE,"E48"),sQuery(id+"F0.wireOp",EDGE,"E49"),sQuery(id+"F0.wireOp",EDGE,"E50"),sQuery(id+"F0.wireOp",EDGE,"E51"),sQuery(id+"F0.wireOp",EDGE,"E52"),sQuery(id+"F0.wireOp",EDGE,"E53"),sQuery(id+"F0.wireOp",EDGE,"E54"),sQuery(id+"F0.wireOp",EDGE,"E55"),sQuery(id+"F0.wireOp",EDGE,"E56"),sQuery(id+"F0.wireOp",EDGE,"E57"),sQuery(id+"F0.wireOp",EDGE,"E58"),sQuery(id+"F0.wireOp",EDGE,"E59"),sQuery(id+"F0.wireOp",EDGE,"E60"),sQuery(id+"F0.wireOp",EDGE,"E61"),sQuery(id+"F0.wireOp",EDGE,"E62"),sQuery(id+"F0.wireOp",EDGE,"E63"),sQuery(id+"F0.wireOp",EDGE,"E64"),sQuery(id+"F0.wireOp",EDGE,"E65"),sQuery(id+"F0.wireOp",EDGE,"E66"),sQuery(id+"F0.wireOp",EDGE,"E67"),sQuery(id+"F0.wireOp",EDGE,"E68"),sQuery(id+"F0.wireOp",EDGE,"E69")])]});
            var Q2;
            Q2=makeQuery(id+"F16.opExtrude","SWEPT_BODY",BODY,{"disambiguationData":[OSD([sQuery(id+"F15.wireOp",EDGE,"E124.0"),sQuery(id+"F15.wireOp",EDGE,"E123.0"),sQuery(id+"F15.wireOp",EDGE,"E125.right"),sQuery(id+"F15.wireOp",EDGE,"E126.0.0"),sQuery(id+"F15.wireOp",EDGE,"E126.0.2"),sQuery(id+"F15.wireOp",EDGE,"E126.0.3"),sQuery(id+"F15.wireOp",EDGE,"E127.0.1"),sQuery(id+"F15.wireOp",EDGE,"E127.0.2"),sQuery(id+"F15.wireOp",EDGE,"E127.0.3"),sQuery(id+"F15.wireOp",EDGE,"E128.0.1"),sQuery(id+"F15.wireOp",EDGE,"E128.0.2"),sQuery(id+"F15.wireOp",EDGE,"E128.0.3"),sQuery(id+"F15.wireOp",EDGE,"E129"),sQuery(id+"F15.wireOp",EDGE,"E130"),sQuery(id+"F15.wireOp",EDGE,"E131"),sQuery(id+"F15.wireOp",EDGE,"E132")])]});
            var Q3;
            Q3=makeQuery(id+"F17.opPattern","COPY",BODY,{"derivedFrom":makeQuery(id+"F16.opExtrude","SWEPT_BODY",BODY,{"disambiguationData":[OSD([sQuery(id+"F15.wireOp",EDGE,"E124.0"),sQuery(id+"F15.wireOp",EDGE,"E123.0"),sQuery(id+"F15.wireOp",EDGE,"E125.right"),sQuery(id+"F15.wireOp",EDGE,"E126.0.0"),sQuery(id+"F15.wireOp",EDGE,"E126.0.2"),sQuery(id+"F15.wireOp",EDGE,"E126.0.3"),sQuery(id+"F15.wireOp",EDGE,"E127.0.1"),sQuery(id+"F15.wireOp",EDGE,"E127.0.2"),sQuery(id+"F15.wireOp",EDGE,"E127.0.3"),sQuery(id+"F15.wireOp",EDGE,"E128.0.1"),sQuery(id+"F15.wireOp",EDGE,"E128.0.2"),sQuery(id+"F15.wireOp",EDGE,"E128.0.3"),sQuery(id+"F15.wireOp",EDGE,"E129"),sQuery(id+"F15.wireOp",EDGE,"E130"),sQuery(id+"F15.wireOp",EDGE,"E131"),sQuery(id+"F15.wireOp",EDGE,"E132")])]}),"instanceName":"1"});
            var Q4;
            Q4=makeQuery(id+"F19.opExtrude","SWEPT_BODY",BODY,{"disambiguationData":[OSD([sQuery(id+"F18.wireOp",EDGE,"E133.0.0"),sQuery(id+"F18.wireOp",EDGE,"E133.0.1"),sQuery(id+"F18.wireOp",EDGE,"E133.0.2"),sQuery(id+"F18.wireOp",EDGE,"E134.0.0"),sQuery(id+"F18.wireOp",EDGE,"E134.0.2"),sQuery(id+"F18.wireOp",EDGE,"E134.0.3"),sQuery(id+"F18.wireOp",EDGE,"E135.0.1"),sQuery(id+"F18.wireOp",EDGE,"E135.0.2"),sQuery(id+"F18.wireOp",EDGE,"E135.0.3"),sQuery(id+"F18.wireOp",EDGE,"E136.0.1"),sQuery(id+"F18.wireOp",EDGE,"E136.0.2"),sQuery(id+"F18.wireOp",EDGE,"E136.0.3"),sQuery(id+"F18.wireOp",EDGE,"E137"),sQuery(id+"F18.wireOp",EDGE,"E138"),sQuery(id+"F18.wireOp",EDGE,"E139"),sQuery(id+"F18.wireOp",EDGE,"E140")])]});
            var Q5;
            Q5=makeQuery(id+"F9.opPattern","COPY",BODY,{"derivedFrom":makeQuery(id+"F1.opExtrude","SWEPT_BODY",BODY,{"disambiguationData":[OSD([sQuery(id+"F0.wireOp",EDGE,"E0"),sQuery(id+"F0.wireOp",EDGE,"E1"),sQuery(id+"F0.wireOp",EDGE,"E2"),sQuery(id+"F0.wireOp",EDGE,"E3"),sQuery(id+"F0.wireOp",EDGE,"E4"),sQuery(id+"F0.wireOp",EDGE,"E5"),sQuery(id+"F0.wireOp",EDGE,"E6"),sQuery(id+"F0.wireOp",EDGE,"E7"),sQuery(id+"F0.wireOp",EDGE,"E8"),sQuery(id+"F0.wireOp",EDGE,"E9"),sQuery(id+"F0.wireOp",EDGE,"E10"),sQuery(id+"F0.wireOp",EDGE,"E11"),sQuery(id+"F0.wireOp",EDGE,"E12"),sQuery(id+"F0.wireOp",EDGE,"E13"),sQuery(id+"F0.wireOp",EDGE,"E14"),sQuery(id+"F0.wireOp",EDGE,"E15"),sQuery(id+"F0.wireOp",EDGE,"E16"),sQuery(id+"F0.wireOp",EDGE,"E17"),sQuery(id+"F0.wireOp",EDGE,"E18"),sQuery(id+"F0.wireOp",EDGE,"E19"),sQuery(id+"F0.wireOp",EDGE,"E20"),sQuery(id+"F0.wireOp",EDGE,"E21"),sQuery(id+"F0.wireOp",EDGE,"E22"),sQuery(id+"F0.wireOp",EDGE,"E23"),sQuery(id+"F0.wireOp",EDGE,"E24"),sQuery(id+"F0.wireOp",EDGE,"E25"),sQuery(id+"F0.wireOp",EDGE,"E26"),sQuery(id+"F0.wireOp",EDGE,"E27"),sQuery(id+"F0.wireOp",EDGE,"E28"),sQuery(id+"F0.wireOp",EDGE,"E29"),sQuery(id+"F0.wireOp",EDGE,"E30"),sQuery(id+"F0.wireOp",EDGE,"E31"),sQuery(id+"F0.wireOp",EDGE,"E32"),sQuery(id+"F0.wireOp",EDGE,"E33"),sQuery(id+"F0.wireOp",EDGE,"E34"),sQuery(id+"F0.wireOp",EDGE,"E35"),sQuery(id+"F0.wireOp",EDGE,"E36"),sQuery(id+"F0.wireOp",EDGE,"E37"),sQuery(id+"F0.wireOp",EDGE,"E38"),sQuery(id+"F0.wireOp",EDGE,"E39"),sQuery(id+"F0.wireOp",EDGE,"E40"),sQuery(id+"F0.wireOp",EDGE,"E41"),sQuery(id+"F0.wireOp",EDGE,"E42"),sQuery(id+"F0.wireOp",EDGE,"E43"),sQuery(id+"F0.wireOp",EDGE,"E44"),sQuery(id+"F0.wireOp",EDGE,"E45"),sQuery(id+"F0.wireOp",EDGE,"E46"),sQuery(id+"F0.wireOp",EDGE,"E47"),sQuery(id+"F0.wireOp",EDGE,"E48"),sQuery(id+"F0.wireOp",EDGE,"E49"),sQuery(id+"F0.wireOp",EDGE,"E50"),sQuery(id+"F0.wireOp",EDGE,"E51"),sQuery(id+"F0.wireOp",EDGE,"E52"),sQuery(id+"F0.wireOp",EDGE,"E53"),sQuery(id+"F0.wireOp",EDGE,"E54"),sQuery(id+"F0.wireOp",EDGE,"E55"),sQuery(id+"F0.wireOp",EDGE,"E56"),sQuery(id+"F0.wireOp",EDGE,"E57"),sQuery(id+"F0.wireOp",EDGE,"E58"),sQuery(id+"F0.wireOp",EDGE,"E59"),sQuery(id+"F0.wireOp",EDGE,"E60"),sQuery(id+"F0.wireOp",EDGE,"E61"),sQuery(id+"F0.wireOp",EDGE,"E62"),sQuery(id+"F0.wireOp",EDGE,"E63"),sQuery(id+"F0.wireOp",EDGE,"E64"),sQuery(id+"F0.wireOp",EDGE,"E65"),sQuery(id+"F0.wireOp",EDGE,"E66"),sQuery(id+"F0.wireOp",EDGE,"E67"),sQuery(id+"F0.wireOp",EDGE,"E68"),sQuery(id+"F0.wireOp",EDGE,"E69")])]}),"instanceName":"1"});
            transform(context, id + "F21", {"entities" : qUnion([Q0, Q1, Q2, Q3, Q4, Q5]), "transformType" : TransformType.TRANSLATION_3D, "dx" : 0 * mm, "dy" : 254 * mm, "dz" : 0 * mm, "makeCopy" : true});
        }
        {
            var Q0;
            Q0=qCreatedBy(makeId("Top.planeOp"),FACE);
            var sketch = newSketch(context, id + "F22", { "sketchPlane" : qUnion([Q0])});
            skLineSegment(sketch, "E141.0", {"start": v(-176.53, 232.12) * mm, "end": v(-176.53, 194.3) * mm});
            skLineSegment(sketch, "E142", {"start": v(-198.37, 213.2) * mm, "end": v(-110.34, 213.2) * mm});
            skPoint(sketch, "E142.startSnap0", {"position": v(-176.53, 213.2) * mm});
            skPoint(sketch, "E142.endSnap0", {"position": v(-176.53, 213.2) * mm});
            skSolve(sketch);
        }
        {
            var Q0;
            Q0=makeQuery(id+"F21.opPattern","COPY",BODY,{"derivedFrom":makeQuery(id+"F6.opPattern","COPY",BODY,{"derivedFrom":makeQuery(id+"F1.opExtrude","SWEPT_BODY",BODY,{"disambiguationData":[OSD([sQuery(id+"F0.wireOp",EDGE,"E0"),sQuery(id+"F0.wireOp",EDGE,"E1"),sQuery(id+"F0.wireOp",EDGE,"E2"),sQuery(id+"F0.wireOp",EDGE,"E3"),sQuery(id+"F0.wireOp",EDGE,"E4"),sQuery(id+"F0.wireOp",EDGE,"E5"),sQuery(id+"F0.wireOp",EDGE,"E6"),sQuery(id+"F0.wireOp",EDGE,"E7"),sQuery(id+"F0.wireOp",EDGE,"E8"),sQuery(id+"F0.wireOp",EDGE,"E9"),sQuery(id+"F0.wireOp",EDGE,"E10"),sQuery(id+"F0.wireOp",EDGE,"E11"),sQuery(id+"F0.wireOp",EDGE,"E12"),sQuery(id+"F0.wireOp",EDGE,"E13"),sQuery(id+"F0.wireOp",EDGE,"E14"),sQuery(id+"F0.wireOp",EDGE,"E15"),sQuery(id+"F0.wireOp",EDGE,"E16"),sQuery(id+"F0.wireOp",EDGE,"E17"),sQuery(id+"F0.wireOp",EDGE,"E18"),sQuery(id+"F0.wireOp",EDGE,"E19"),sQuery(id+"F0.wireOp",EDGE,"E20"),sQuery(id+"F0.wireOp",EDGE,"E21"),sQuery(id+"F0.wireOp",EDGE,"E22"),sQuery(id+"F0.wireOp",EDGE,"E23"),sQuery(id+"F0.wireOp",EDGE,"E24"),sQuery(id+"F0.wireOp",EDGE,"E25"),sQuery(id+"F0.wireOp",EDGE,"E26"),sQuery(id+"F0.wireOp",EDGE,"E27"),sQuery(id+"F0.wireOp",EDGE,"E28"),sQuery(id+"F0.wireOp",EDGE,"E29"),sQuery(id+"F0.wireOp",EDGE,"E30"),sQuery(id+"F0.wireOp",EDGE,"E31"),sQuery(id+"F0.wireOp",EDGE,"E32"),sQuery(id+"F0.wireOp",EDGE,"E33"),sQuery(id+"F0.wireOp",EDGE,"E34"),sQuery(id+"F0.wireOp",EDGE,"E35"),sQuery(id+"F0.wireOp",EDGE,"E36"),sQuery(id+"F0.wireOp",EDGE,"E37"),sQuery(id+"F0.wireOp",EDGE,"E38"),sQuery(id+"F0.wireOp",EDGE,"E39"),sQuery(id+"F0.wireOp",EDGE,"E40"),sQuery(id+"F0.wireOp",EDGE,"E41"),sQuery(id+"F0.wireOp",EDGE,"E42"),sQuery(id+"F0.wireOp",EDGE,"E43"),sQuery(id+"F0.wireOp",EDGE,"E44"),sQuery(id+"F0.wireOp",EDGE,"E45"),sQuery(id+"F0.wireOp",EDGE,"E46"),sQuery(id+"F0.wireOp",EDGE,"E47"),sQuery(id+"F0.wireOp",EDGE,"E48"),sQuery(id+"F0.wireOp",EDGE,"E49"),sQuery(id+"F0.wireOp",EDGE,"E50"),sQuery(id+"F0.wireOp",EDGE,"E51"),sQuery(id+"F0.wireOp",EDGE,"E52"),sQuery(id+"F0.wireOp",EDGE,"E53"),sQuery(id+"F0.wireOp",EDGE,"E54"),sQuery(id+"F0.wireOp",EDGE,"E55"),sQuery(id+"F0.wireOp",EDGE,"E56"),sQuery(id+"F0.wireOp",EDGE,"E57"),sQuery(id+"F0.wireOp",EDGE,"E58"),sQuery(id+"F0.wireOp",EDGE,"E59"),sQuery(id+"F0.wireOp",EDGE,"E60"),sQuery(id+"F0.wireOp",EDGE,"E61"),sQuery(id+"F0.wireOp",EDGE,"E62"),sQuery(id+"F0.wireOp",EDGE,"E63"),sQuery(id+"F0.wireOp",EDGE,"E64"),sQuery(id+"F0.wireOp",EDGE,"E65"),sQuery(id+"F0.wireOp",EDGE,"E66"),sQuery(id+"F0.wireOp",EDGE,"E67"),sQuery(id+"F0.wireOp",EDGE,"E68"),sQuery(id+"F0.wireOp",EDGE,"E69")])]}),"instanceName":"1"}),"instanceName":"1"});
            var Q1;
            Q1=makeQuery(id+"F21.opPattern","COPY",BODY,{"derivedFrom":makeQuery(id+"F16.opExtrude","SWEPT_BODY",BODY,{"disambiguationData":[OSD([sQuery(id+"F15.wireOp",EDGE,"E124.0"),sQuery(id+"F15.wireOp",EDGE,"E123.0"),sQuery(id+"F15.wireOp",EDGE,"E125.right"),sQuery(id+"F15.wireOp",EDGE,"E126.0.0"),sQuery(id+"F15.wireOp",EDGE,"E126.0.2"),sQuery(id+"F15.wireOp",EDGE,"E126.0.3"),sQuery(id+"F15.wireOp",EDGE,"E127.0.1"),sQuery(id+"F15.wireOp",EDGE,"E127.0.2"),sQuery(id+"F15.wireOp",EDGE,"E127.0.3"),sQuery(id+"F15.wireOp",EDGE,"E128.0.1"),sQuery(id+"F15.wireOp",EDGE,"E128.0.2"),sQuery(id+"F15.wireOp",EDGE,"E128.0.3"),sQuery(id+"F15.wireOp",EDGE,"E129"),sQuery(id+"F15.wireOp",EDGE,"E130"),sQuery(id+"F15.wireOp",EDGE,"E131"),sQuery(id+"F15.wireOp",EDGE,"E132")])]}),"instanceName":"1"});
            var Q2;
            Q2=makeQuery(id+"F21.opPattern","COPY",BODY,{"derivedFrom":makeQuery(id+"F1.opExtrude","SWEPT_BODY",BODY,{"disambiguationData":[OSD([sQuery(id+"F0.wireOp",EDGE,"E0"),sQuery(id+"F0.wireOp",EDGE,"E1"),sQuery(id+"F0.wireOp",EDGE,"E2"),sQuery(id+"F0.wireOp",EDGE,"E3"),sQuery(id+"F0.wireOp",EDGE,"E4"),sQuery(id+"F0.wireOp",EDGE,"E5"),sQuery(id+"F0.wireOp",EDGE,"E6"),sQuery(id+"F0.wireOp",EDGE,"E7"),sQuery(id+"F0.wireOp",EDGE,"E8"),sQuery(id+"F0.wireOp",EDGE,"E9"),sQuery(id+"F0.wireOp",EDGE,"E10"),sQuery(id+"F0.wireOp",EDGE,"E11"),sQuery(id+"F0.wireOp",EDGE,"E12"),sQuery(id+"F0.wireOp",EDGE,"E13"),sQuery(id+"F0.wireOp",EDGE,"E14"),sQuery(id+"F0.wireOp",EDGE,"E15"),sQuery(id+"F0.wireOp",EDGE,"E16"),sQuery(id+"F0.wireOp",EDGE,"E17"),sQuery(id+"F0.wireOp",EDGE,"E18"),sQuery(id+"F0.wireOp",EDGE,"E19"),sQuery(id+"F0.wireOp",EDGE,"E20"),sQuery(id+"F0.wireOp",EDGE,"E21"),sQuery(id+"F0.wireOp",EDGE,"E22"),sQuery(id+"F0.wireOp",EDGE,"E23"),sQuery(id+"F0.wireOp",EDGE,"E24"),sQuery(id+"F0.wireOp",EDGE,"E25"),sQuery(id+"F0.wireOp",EDGE,"E26"),sQuery(id+"F0.wireOp",EDGE,"E27"),sQuery(id+"F0.wireOp",EDGE,"E28"),sQuery(id+"F0.wireOp",EDGE,"E29"),sQuery(id+"F0.wireOp",EDGE,"E30"),sQuery(id+"F0.wireOp",EDGE,"E31"),sQuery(id+"F0.wireOp",EDGE,"E32"),sQuery(id+"F0.wireOp",EDGE,"E33"),sQuery(id+"F0.wireOp",EDGE,"E34"),sQuery(id+"F0.wireOp",EDGE,"E35"),sQuery(id+"F0.wireOp",EDGE,"E36"),sQuery(id+"F0.wireOp",EDGE,"E37"),sQuery(id+"F0.wireOp",EDGE,"E38"),sQuery(id+"F0.wireOp",EDGE,"E39"),sQuery(id+"F0.wireOp",EDGE,"E40"),sQuery(id+"F0.wireOp",EDGE,"E41"),sQuery(id+"F0.wireOp",EDGE,"E42"),sQuery(id+"F0.wireOp",EDGE,"E43"),sQuery(id+"F0.wireOp",EDGE,"E44"),sQuery(id+"F0.wireOp",EDGE,"E45"),sQuery(id+"F0.wireOp",EDGE,"E46"),sQuery(id+"F0.wireOp",EDGE,"E47"),sQuery(id+"F0.wireOp",EDGE,"E48"),sQuery(id+"F0.wireOp",EDGE,"E49"),sQuery(id+"F0.wireOp",EDGE,"E50"),sQuery(id+"F0.wireOp",EDGE,"E51"),sQuery(id+"F0.wireOp",EDGE,"E52"),sQuery(id+"F0.wireOp",EDGE,"E53"),sQuery(id+"F0.wireOp",EDGE,"E54"),sQuery(id+"F0.wireOp",EDGE,"E55"),sQuery(id+"F0.wireOp",EDGE,"E56"),sQuery(id+"F0.wireOp",EDGE,"E57"),sQuery(id+"F0.wireOp",EDGE,"E58"),sQuery(id+"F0.wireOp",EDGE,"E59"),sQuery(id+"F0.wireOp",EDGE,"E60"),sQuery(id+"F0.wireOp",EDGE,"E61"),sQuery(id+"F0.wireOp",EDGE,"E62"),sQuery(id+"F0.wireOp",EDGE,"E63"),sQuery(id+"F0.wireOp",EDGE,"E64"),sQuery(id+"F0.wireOp",EDGE,"E65"),sQuery(id+"F0.wireOp",EDGE,"E66"),sQuery(id+"F0.wireOp",EDGE,"E67"),sQuery(id+"F0.wireOp",EDGE,"E68"),sQuery(id+"F0.wireOp",EDGE,"E69")])]}),"instanceName":"1"});
            var Q3;
            Q3=makeQuery(id+"F21.opPattern","COPY",BODY,{"derivedFrom":makeQuery(id+"F19.opExtrude","SWEPT_BODY",BODY,{"disambiguationData":[OSD([sQuery(id+"F18.wireOp",EDGE,"E133.0.0"),sQuery(id+"F18.wireOp",EDGE,"E133.0.1"),sQuery(id+"F18.wireOp",EDGE,"E133.0.2"),sQuery(id+"F18.wireOp",EDGE,"E134.0.0"),sQuery(id+"F18.wireOp",EDGE,"E134.0.2"),sQuery(id+"F18.wireOp",EDGE,"E134.0.3"),sQuery(id+"F18.wireOp",EDGE,"E135.0.1"),sQuery(id+"F18.wireOp",EDGE,"E135.0.2"),sQuery(id+"F18.wireOp",EDGE,"E135.0.3"),sQuery(id+"F18.wireOp",EDGE,"E136.0.1"),sQuery(id+"F18.wireOp",EDGE,"E136.0.2"),sQuery(id+"F18.wireOp",EDGE,"E136.0.3"),sQuery(id+"F18.wireOp",EDGE,"E137"),sQuery(id+"F18.wireOp",EDGE,"E138"),sQuery(id+"F18.wireOp",EDGE,"E139"),sQuery(id+"F18.wireOp",EDGE,"E140")])]}),"instanceName":"1"});
            var Q4;
            Q4=makeQuery(id+"F21.opPattern","COPY",BODY,{"derivedFrom":makeQuery(id+"F17.opPattern","COPY",BODY,{"derivedFrom":makeQuery(id+"F16.opExtrude","SWEPT_BODY",BODY,{"disambiguationData":[OSD([sQuery(id+"F15.wireOp",EDGE,"E124.0"),sQuery(id+"F15.wireOp",EDGE,"E123.0"),sQuery(id+"F15.wireOp",EDGE,"E125.right"),sQuery(id+"F15.wireOp",EDGE,"E126.0.0"),sQuery(id+"F15.wireOp",EDGE,"E126.0.2"),sQuery(id+"F15.wireOp",EDGE,"E126.0.3"),sQuery(id+"F15.wireOp",EDGE,"E127.0.1"),sQuery(id+"F15.wireOp",EDGE,"E127.0.2"),sQuery(id+"F15.wireOp",EDGE,"E127.0.3"),sQuery(id+"F15.wireOp",EDGE,"E128.0.1"),sQuery(id+"F15.wireOp",EDGE,"E128.0.2"),sQuery(id+"F15.wireOp",EDGE,"E128.0.3"),sQuery(id+"F15.wireOp",EDGE,"E129"),sQuery(id+"F15.wireOp",EDGE,"E130"),sQuery(id+"F15.wireOp",EDGE,"E131"),sQuery(id+"F15.wireOp",EDGE,"E132")])]}),"instanceName":"1"}),"instanceName":"1"});
            var Q5;
            Q5=makeQuery(id+"F21.opPattern","COPY",BODY,{"derivedFrom":makeQuery(id+"F9.opPattern","COPY",BODY,{"derivedFrom":makeQuery(id+"F1.opExtrude","SWEPT_BODY",BODY,{"disambiguationData":[OSD([sQuery(id+"F0.wireOp",EDGE,"E0"),sQuery(id+"F0.wireOp",EDGE,"E1"),sQuery(id+"F0.wireOp",EDGE,"E2"),sQuery(id+"F0.wireOp",EDGE,"E3"),sQuery(id+"F0.wireOp",EDGE,"E4"),sQuery(id+"F0.wireOp",EDGE,"E5"),sQuery(id+"F0.wireOp",EDGE,"E6"),sQuery(id+"F0.wireOp",EDGE,"E7"),sQuery(id+"F0.wireOp",EDGE,"E8"),sQuery(id+"F0.wireOp",EDGE,"E9"),sQuery(id+"F0.wireOp",EDGE,"E10"),sQuery(id+"F0.wireOp",EDGE,"E11"),sQuery(id+"F0.wireOp",EDGE,"E12"),sQuery(id+"F0.wireOp",EDGE,"E13"),sQuery(id+"F0.wireOp",EDGE,"E14"),sQuery(id+"F0.wireOp",EDGE,"E15"),sQuery(id+"F0.wireOp",EDGE,"E16"),sQuery(id+"F0.wireOp",EDGE,"E17"),sQuery(id+"F0.wireOp",EDGE,"E18"),sQuery(id+"F0.wireOp",EDGE,"E19"),sQuery(id+"F0.wireOp",EDGE,"E20"),sQuery(id+"F0.wireOp",EDGE,"E21"),sQuery(id+"F0.wireOp",EDGE,"E22"),sQuery(id+"F0.wireOp",EDGE,"E23"),sQuery(id+"F0.wireOp",EDGE,"E24"),sQuery(id+"F0.wireOp",EDGE,"E25"),sQuery(id+"F0.wireOp",EDGE,"E26"),sQuery(id+"F0.wireOp",EDGE,"E27"),sQuery(id+"F0.wireOp",EDGE,"E28"),sQuery(id+"F0.wireOp",EDGE,"E29"),sQuery(id+"F0.wireOp",EDGE,"E30"),sQuery(id+"F0.wireOp",EDGE,"E31"),sQuery(id+"F0.wireOp",EDGE,"E32"),sQuery(id+"F0.wireOp",EDGE,"E33"),sQuery(id+"F0.wireOp",EDGE,"E34"),sQuery(id+"F0.wireOp",EDGE,"E35"),sQuery(id+"F0.wireOp",EDGE,"E36"),sQuery(id+"F0.wireOp",EDGE,"E37"),sQuery(id+"F0.wireOp",EDGE,"E38"),sQuery(id+"F0.wireOp",EDGE,"E39"),sQuery(id+"F0.wireOp",EDGE,"E40"),sQuery(id+"F0.wireOp",EDGE,"E41"),sQuery(id+"F0.wireOp",EDGE,"E42"),sQuery(id+"F0.wireOp",EDGE,"E43"),sQuery(id+"F0.wireOp",EDGE,"E44"),sQuery(id+"F0.wireOp",EDGE,"E45"),sQuery(id+"F0.wireOp",EDGE,"E46"),sQuery(id+"F0.wireOp",EDGE,"E47"),sQuery(id+"F0.wireOp",EDGE,"E48"),sQuery(id+"F0.wireOp",EDGE,"E49"),sQuery(id+"F0.wireOp",EDGE,"E50"),sQuery(id+"F0.wireOp",EDGE,"E51"),sQuery(id+"F0.wireOp",EDGE,"E52"),sQuery(id+"F0.wireOp",EDGE,"E53"),sQuery(id+"F0.wireOp",EDGE,"E54"),sQuery(id+"F0.wireOp",EDGE,"E55"),sQuery(id+"F0.wireOp",EDGE,"E56"),sQuery(id+"F0.wireOp",EDGE,"E57"),sQuery(id+"F0.wireOp",EDGE,"E58"),sQuery(id+"F0.wireOp",EDGE,"E59"),sQuery(id+"F0.wireOp",EDGE,"E60"),sQuery(id+"F0.wireOp",EDGE,"E61"),sQuery(id+"F0.wireOp",EDGE,"E62"),sQuery(id+"F0.wireOp",EDGE,"E63"),sQuery(id+"F0.wireOp",EDGE,"E64"),sQuery(id+"F0.wireOp",EDGE,"E65"),sQuery(id+"F0.wireOp",EDGE,"E66"),sQuery(id+"F0.wireOp",EDGE,"E67"),sQuery(id+"F0.wireOp",EDGE,"E68"),sQuery(id+"F0.wireOp",EDGE,"E69")])]}),"instanceName":"1"}),"instanceName":"1"});
            var Q6;
            Q6=sQuery(id+"F22.wireOp",EDGE,"E142");
            transform(context, id + "F23", {"entities" : qUnion([Q0, Q1, Q2, Q3, Q4, Q5]), "transformType" : TransformType.ROTATION, "transformAxis" : qUnion([Q6]), "angle" : 90 * degree, "makeCopy" : false});
        }
    });
